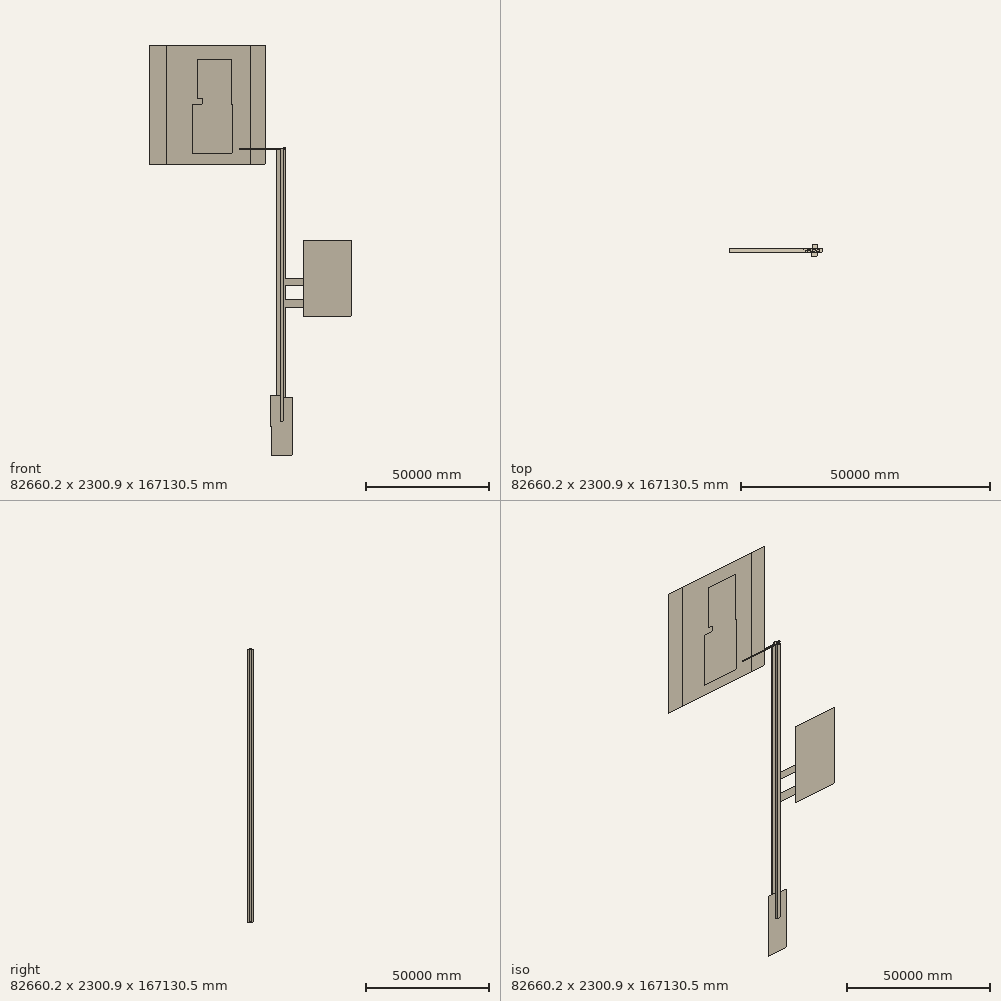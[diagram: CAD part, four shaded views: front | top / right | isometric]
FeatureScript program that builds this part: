
annotation { "Feature Type Name" : "Feature", "Feature Type Description" : "" }
export const myFeature = defineFeature(function(context is Context, id is Id, definition is map)
    precondition{}
    {
        {
            var Q0;
            Q0=qCreatedBy(makeId("Front.planeOp"),FACE);
            var sketch = newSketch(context, id + "F0", { "sketchPlane" : qUnion([Q0])});
            skLineSegment(sketch, "E0.bottom", {"start": v(-96.08, 96.62) * mm, "end": v(94.95, 96.62) * mm});
            skLineSegment(sketch, "E0.top", {"start": v(-96.08, -96.37) * mm, "end": v(94.95, -96.37) * mm});
            skLineSegment(sketch, "E0.left", {"start": v(-96.08, 96.62) * mm, "end": v(-96.08, -96.37) * mm});
            skLineSegment(sketch, "E0.right", {"start": v(94.95, 96.62) * mm, "end": v(94.95, -96.37) * mm});
            skSolve(sketch);
        }
        {
            var Q0;
            Q0 = qSketchRegion(id + "F0", true);
            extrude(context, id + "F1", {"entities" : qUnion([Q0]), "depth" : 25.4 * mm, "offsetDistance" : 25.4 * mm});
        }
        {
            var Q0;
            Q0=makeQuery(id+"F1.opExtrude","CAP_FACE",FACE,{"disambiguationData":[OSD([sQuery(id+"F0.wireOp",EDGE,"E0.bottom"),sQuery(id+"F0.wireOp",EDGE,"E0.top"),sQuery(id+"F0.wireOp",EDGE,"E0.left"),sQuery(id+"F0.wireOp",EDGE,"E0.right")])],"isStart":true});
            var sketch = newSketch(context, id + "F2", { "sketchPlane" : qUnion([Q0])});
            skLineSegment(sketch, "E1.bottom", {"start": v(0, 0) * mm, "end": v(76.12, 0) * mm});
            skLineSegment(sketch, "E1.top", {"start": v(0, 76.11) * mm, "end": v(76.12, 76.11) * mm});
            skLineSegment(sketch, "E1.left", {"start": v(0, 0) * mm, "end": v(0, 76.11) * mm});
            skLineSegment(sketch, "E1.right", {"start": v(76.12, 0) * mm, "end": v(76.12, 76.11) * mm});
            skLineSegment(sketch, "E2.bottom", {"start": v(76.12, 76.11) * mm, "end": v(-77.23, 76.11) * mm});
            skLineSegment(sketch, "E2.top", {"start": v(76.12, -75.62) * mm, "end": v(-77.23, -75.62) * mm});
            skLineSegment(sketch, "E2.left", {"start": v(76.12, 76.11) * mm, "end": v(76.12, -75.62) * mm});
            skLineSegment(sketch, "E2.right", {"start": v(-77.23, 76.11) * mm, "end": v(-77.23, -75.62) * mm});
            skSolve(sketch);
        }
        {
            var Q0;
            Q0 = qSketchRegion(id + "F2", true);
            extrude(context, id + "F3", {"entities" : qUnion([Q0]), "operationType" : NewBodyOperationType.ADD, "depth" : 25.4 * mm, "offsetDistance" : 25.4 * mm});
        }
        {
            var Q0;
            Q0=makeQuery(id+"F3.opExtrude","CAP_FACE",FACE,{"disambiguationData":[OSD([sQuery(id+"F2.wireOp",EDGE,"E2.bottom"),sQuery(id+"F2.wireOp",EDGE,"E2.top"),sQuery(id+"F2.wireOp",EDGE,"E2.left"),sQuery(id+"F2.wireOp",EDGE,"E2.right")])],"isStart":false});
            var sketch = newSketch(context, id + "F4", { "sketchPlane" : qUnion([Q0])});
            skLineSegment(sketch, "E3.bottom", {"start": v(97.63, 126.48) * mm, "end": v(-70.35, 126.48) * mm});
            skLineSegment(sketch, "E3.top", {"start": v(97.63, -97.82) * mm, "end": v(-70.35, -97.82) * mm});
            skLineSegment(sketch, "E3.left", {"start": v(97.63, 126.48) * mm, "end": v(97.63, -97.82) * mm});
            skLineSegment(sketch, "E3.right", {"start": v(-70.35, 126.48) * mm, "end": v(-70.35, -97.82) * mm});
            skLineSegment(sketch, "E4.bottom", {"start": v(-70.35, -97.82) * mm, "end": v(-97.74, -97.82) * mm});
            skLineSegment(sketch, "E4.top", {"start": v(-70.35, 96.2) * mm, "end": v(-97.74, 96.2) * mm});
            skLineSegment(sketch, "E4.left", {"start": v(-70.35, -97.82) * mm, "end": v(-70.35, 96.2) * mm});
            skLineSegment(sketch, "E4.right", {"start": v(-97.74, -97.82) * mm, "end": v(-97.74, 96.2) * mm});
            skSolve(sketch);
        }
        {
            var Q0;
            Q0 = qSketchRegion(id + "F4", true);
            extrude(context, id + "F5", {"entities" : qUnion([Q0]), "operationType" : NewBodyOperationType.ADD, "depth" : 25.4 * mm, "offsetDistance" : 25.4 * mm});
        }
        {
            var Q0;
            Q0=makeQuery(id+"F5.opExtrude","SWEPT_FACE",FACE,{"disambiguationData":[OSD([sQuery(id+"F4.wireOp",EDGE,"E4.top")])]});
            var sketch = newSketch(context, id + "F6", { "sketchPlane" : qUnion([Q0])});
            skLineSegment(sketch, "E5", {"start": v(97.74, 50.8) * mm, "end": v(97.74, 0) * mm});
            skLineSegment(sketch, "E6", {"start": v(97.74, 0) * mm, "end": v(48.7, -15.21) * mm});
            skLineSegment(sketch, "E7", {"start": v(48.7, -15.21) * mm, "end": v(97.74, 50.8) * mm});
            skLineSegment(sketch, "E8", {"start": v(48.7, -15.21) * mm, "end": v(70.35, 50.8) * mm});
            skSolve(sketch);
        }
        {
            var Q0;
            Q0 = qSketchRegion(id + "F6", true);
            extrude(context, id + "F7", {"entities" : qUnion([Q0]), "operationType" : NewBodyOperationType.ADD, "depth" : 25.4 * mm, "offsetDistance" : 25.4 * mm});
        }
        {
            var Q0;
            Q0=makeQuery(id+"F7.opExtrude","SWEPT_FACE",FACE,{"disambiguationData":[OSD([sQuery(id+"F6.wireOp",EDGE,"E7")])]});
            var sketch = newSketch(context, id + "F8", { "sketchPlane" : qUnion([Q0])});
            skLineSegment(sketch, "E9.bottom", {"start": v(-153.7, 205.91) * mm, "end": v(22.33, 205.91) * mm});
            skLineSegment(sketch, "E9.top", {"start": v(-153.7, 15.9) * mm, "end": v(22.33, 15.9) * mm});
            skLineSegment(sketch, "E9.left", {"start": v(-153.7, 205.91) * mm, "end": v(-153.7, 15.9) * mm});
            skLineSegment(sketch, "E9.right", {"start": v(22.33, 205.91) * mm, "end": v(22.33, 15.9) * mm});
            skLineSegment(sketch, "E10.bottom", {"start": v(22.33, 168.8) * mm, "end": v(22.33, 168.8) * mm});
            skLineSegment(sketch, "E10.top", {"start": v(22.33, 27.02) * mm, "end": v(22.33, 27.02) * mm});
            skLineSegment(sketch, "E10.left", {"start": v(22.33, 168.8) * mm, "end": v(22.33, 27.02) * mm});
            skLineSegment(sketch, "E10.right", {"start": v(22.33, 168.8) * mm, "end": v(22.33, 27.02) * mm});
            skSolve(sketch);
        }
        {
            var Q0;
            Q0 = qSketchRegion(id + "F8", true);
            extrude(context, id + "F9", {"entities" : qUnion([Q0]), "operationType" : NewBodyOperationType.ADD, "depth" : 25.4 * mm, "offsetDistance" : 25.4 * mm});
        }
        {
            var Q0;
            {var subQ0=sQuery(id+"F8.wireOp",EDGE,"E9.left");var subQ2=sQuery(id+"F8.wireOp",EDGE,"E9.bottom");var subQ5=sQuery(id+"F0.wireOp",EDGE,"E0.bottom");var subQ6=sQuery(id+"F8.wireOp",EDGE,"E9.top");var subQ7=sQuery(id+"F8.wireOp",EDGE,"E10.right");var subQ8=sQuery(id+"F8.wireOp",EDGE,"E9.right");Q0=makeQuery(id+"F9.boolean.opBoolean","SPLIT",FACE,{"disambiguationData":[TD([makeQuery(id+"F1.opExtrude","SWEPT_FACE",FACE,{"disambiguationData":[OSD([subQ5])]})])],"derivedFrom":makeQuery(id+"F9.opExtrude","CAP_FACE",FACE,{"disambiguationData":[OSD([subQ2,subQ6,subQ0,subQ8,subQ7])],"isStart":true})});}
            var sketch = newSketch(context, id + "F10", { "sketchPlane" : qUnion([Q0])});
            skLineSegment(sketch, "E11.bottom", {"start": v(-30.73, 15.9) * mm, "end": v(163.94, 15.9) * mm});
            skLineSegment(sketch, "E11.top", {"start": v(-30.73, 183.37) * mm, "end": v(163.94, 183.37) * mm});
            skLineSegment(sketch, "E11.left", {"start": v(-30.73, 15.9) * mm, "end": v(-30.73, 183.37) * mm});
            skLineSegment(sketch, "E11.right", {"start": v(163.94, 15.9) * mm, "end": v(163.94, 183.37) * mm});
            skLineSegment(sketch, "E12.bottom", {"start": v(-30.73, 183.37) * mm, "end": v(160.37, 183.37) * mm});
            skLineSegment(sketch, "E12.top", {"start": v(-30.73, 216.06) * mm, "end": v(160.37, 216.06) * mm});
            skLineSegment(sketch, "E12.left", {"start": v(-30.73, 183.37) * mm, "end": v(-30.73, 216.06) * mm});
            skLineSegment(sketch, "E12.right", {"start": v(160.37, 183.37) * mm, "end": v(160.37, 216.06) * mm});
            skSolve(sketch);
        }
        {
            var Q0;
            Q0 = qSketchRegion(id + "F10", true);
            extrude(context, id + "F11", {"entities" : qUnion([Q0]), "operationType" : NewBodyOperationType.ADD, "depth" : 25.4 * mm, "offsetDistance" : 25.4 * mm});
        }
        {
            var Q0;
            Q0=makeQuery(id+"F1.opExtrude","CAP_FACE",FACE,{"disambiguationData":[OSD([sQuery(id+"F0.wireOp",EDGE,"E0.bottom"),sQuery(id+"F0.wireOp",EDGE,"E0.top"),sQuery(id+"F0.wireOp",EDGE,"E0.left"),sQuery(id+"F0.wireOp",EDGE,"E0.right")])],"isStart":false});
            var sketch = newSketch(context, id + "F12", { "sketchPlane" : qUnion([Q0])});
            skLineSegment(sketch, "E13.bottom", {"start": v(0, 0) * mm, "end": v(9.48, 0) * mm});
            skLineSegment(sketch, "E13.top", {"start": v(0, 96.62) * mm, "end": v(9.48, 96.62) * mm});
            skLineSegment(sketch, "E13.left", {"start": v(0, 0) * mm, "end": v(0, 96.62) * mm});
            skLineSegment(sketch, "E13.right", {"start": v(9.48, 0) * mm, "end": v(9.48, 96.62) * mm});
            skLineSegment(sketch, "E14.bottom", {"start": v(9.48, 0) * mm, "end": v(-96.08, 0) * mm});
            skLineSegment(sketch, "E14.top", {"start": v(9.48, -96.37) * mm, "end": v(-96.08, -96.37) * mm});
            skLineSegment(sketch, "E14.left", {"start": v(9.48, 0) * mm, "end": v(9.48, -96.37) * mm});
            skLineSegment(sketch, "E14.right", {"start": v(-96.08, 0) * mm, "end": v(-96.08, -96.37) * mm});
            skLineSegment(sketch, "E15", {"start": v(9.48, 96.62) * mm, "end": v(-27.1, -27.97) * mm});
            skLineSegment(sketch, "E16", {"start": v(-27.1, -27.97) * mm, "end": v(44.8, -104.88) * mm});
            skLineSegment(sketch, "E17", {"start": v(44.8, -104.88) * mm, "end": v(125.25, -29.66) * mm});
            skLineSegment(sketch, "E18", {"start": v(125.25, -29.66) * mm, "end": v(80.32, 0) * mm});
            skLineSegment(sketch, "E19", {"start": v(80.32, 0) * mm, "end": v(9.48, 96.62) * mm});
            skSolve(sketch);
        }
        {
            var Q0;
            Q0 = qSketchRegion(id + "F12", true);
            extrude(context, id + "F13", {"entities" : qUnion([Q0]), "operationType" : NewBodyOperationType.ADD, "depth" : 25.4 * mm, "offsetDistance" : 25.4 * mm});
        }
        {
            var Q0;
            {var subQ0=sQuery(id+"F0.wireOp",EDGE,"E0.left");var subQ1=sQuery(id+"F0.wireOp",EDGE,"E0.bottom");Q0=makeQuery(id+"F13.boolean.opBoolean","SPLIT",FACE,{"disambiguationData":[TD([makeQuery(id+"F1.opExtrude","SWEPT_FACE",FACE,{"disambiguationData":[OSD([subQ0])]})])],"derivedFrom":makeQuery(id+"F1.opExtrude","CAP_FACE",FACE,{"disambiguationData":[OSD([subQ1,sQuery(id+"F0.wireOp",EDGE,"E0.top"),subQ0,sQuery(id+"F0.wireOp",EDGE,"E0.right")])],"isStart":false})});}
            var sketch = newSketch(context, id + "F14", { "sketchPlane" : qUnion([Q0])});
            skCircle(sketch, "E20", {"center": v(-47.68, 49.78) * mm, "radius": 38.28 * mm});
            skLineSegment(sketch, "E21.bottom", {"start": v(-18.9, 0) * mm, "end": v(-80.44, 0) * mm});
            skLineSegment(sketch, "E21.top", {"start": v(-18.9, -70.14) * mm, "end": v(-80.44, -70.14) * mm});
            skLineSegment(sketch, "E21.left", {"start": v(-18.9, 0) * mm, "end": v(-18.9, -70.14) * mm});
            skLineSegment(sketch, "E21.right", {"start": v(-80.44, 0) * mm, "end": v(-80.44, -70.14) * mm});
            skSolve(sketch);
        }
        {
            var Q0;
            Q0 = qSketchRegion(id + "F14", true);
            extrude(context, id + "F15", {"entities" : qUnion([Q0]), "operationType" : NewBodyOperationType.ADD, "depth" : 25.4 * mm, "offsetDistance" : 25.4 * mm});
        }
        {
            var Q0;
            Q0=makeQuery(id+"F5.opExtrude","CAP_FACE",FACE,{"disambiguationData":[OSD([sQuery(id+"F4.wireOp",EDGE,"E3.bottom"),sQuery(id+"F4.wireOp",EDGE,"E3.top"),sQuery(id+"F4.wireOp",EDGE,"E3.left"),sQuery(id+"F4.wireOp",EDGE,"E3.right"),sQuery(id+"F4.wireOp",EDGE,"E4.bottom"),sQuery(id+"F4.wireOp",EDGE,"E4.top"),sQuery(id+"F4.wireOp",EDGE,"E4.right")])],"isStart":false});
            var sketch = newSketch(context, id + "F16", { "sketchPlane" : qUnion([Q0])});
            skLineSegment(sketch, "E22.bottom", {"start": v(-9.65, -19.15) * mm, "end": v(-106, -19.15) * mm});
            skLineSegment(sketch, "E22.top", {"start": v(-9.65, 126.48) * mm, "end": v(-106, 126.48) * mm});
            skLineSegment(sketch, "E22.left", {"start": v(-9.65, -19.15) * mm, "end": v(-9.65, 126.48) * mm});
            skLineSegment(sketch, "E22.right", {"start": v(-106, -19.15) * mm, "end": v(-106, 126.48) * mm});
            skLineSegment(sketch, "E23.bottom", {"start": v(-9.65, 126.48) * mm, "end": v(107.3, 126.48) * mm});
            skLineSegment(sketch, "E23.top", {"start": v(-9.65, -78.96) * mm, "end": v(107.3, -78.96) * mm});
            skLineSegment(sketch, "E23.left", {"start": v(-9.65, 126.48) * mm, "end": v(-9.65, -78.96) * mm});
            skLineSegment(sketch, "E23.right", {"start": v(107.3, 126.48) * mm, "end": v(107.3, -78.96) * mm});
            skLineSegment(sketch, "E24.bottom", {"start": v(107.3, -78.96) * mm, "end": v(-106, -78.96) * mm});
            skLineSegment(sketch, "E24.top", {"start": v(107.3, -19.15) * mm, "end": v(-106, -19.15) * mm});
            skLineSegment(sketch, "E24.left", {"start": v(107.3, -78.96) * mm, "end": v(107.3, -19.15) * mm});
            skLineSegment(sketch, "E24.right", {"start": v(-106, -78.96) * mm, "end": v(-106, -19.15) * mm});
            skLineSegment(sketch, "E25.bottom", {"start": v(107.3, -78.96) * mm, "end": v(-107.64, -78.96) * mm});
            skLineSegment(sketch, "E25.top", {"start": v(107.3, -97.82) * mm, "end": v(-107.64, -97.82) * mm});
            skLineSegment(sketch, "E25.left", {"start": v(107.3, -78.96) * mm, "end": v(107.3, -97.82) * mm});
            skLineSegment(sketch, "E25.right", {"start": v(-107.64, -78.96) * mm, "end": v(-107.64, -97.82) * mm});
            skSolve(sketch);
        }
        {
            var Q0;
            Q0 = qSketchRegion(id + "F16", true);
            extrude(context, id + "F17", {"entities" : qUnion([Q0]), "operationType" : NewBodyOperationType.ADD, "depth" : 25.4 * mm, "offsetDistance" : 25.4 * mm});
        }
        {
            var Q0;
            Q0=makeQuery(id+"F17.opExtrude","CAP_FACE",FACE,{"disambiguationData":[OSD([sQuery(id+"F16.wireOp",EDGE,"E22.top"),sQuery(id+"F16.wireOp",EDGE,"E22.right"),sQuery(id+"F16.wireOp",EDGE,"E23.bottom"),sQuery(id+"F16.wireOp",EDGE,"E23.right"),sQuery(id+"F16.wireOp",EDGE,"E24.left"),sQuery(id+"F16.wireOp",EDGE,"E24.right"),sQuery(id+"F16.wireOp",EDGE,"E25.bottom"),sQuery(id+"F16.wireOp",EDGE,"E25.top"),sQuery(id+"F16.wireOp",EDGE,"E25.left"),sQuery(id+"F16.wireOp",EDGE,"E25.right")])],"isStart":false});
            var sketch = newSketch(context, id + "F18", { "sketchPlane" : qUnion([Q0])});
            skLineSegment(sketch, "E26.bottom", {"start": v(107.3, 126.48) * mm, "end": v(-107.64, 126.48) * mm});
            skLineSegment(sketch, "E26.top", {"start": v(107.3, -88.39) * mm, "end": v(-107.64, -88.39) * mm});
            skLineSegment(sketch, "E26.left", {"start": v(107.3, 126.48) * mm, "end": v(107.3, -88.39) * mm});
            skLineSegment(sketch, "E26.right", {"start": v(-107.64, 126.48) * mm, "end": v(-107.64, -88.39) * mm});
            skLineSegment(sketch, "E27.bottom", {"start": v(-107.64, 126.48) * mm, "end": v(63.7, 126.48) * mm});
            skLineSegment(sketch, "E27.top", {"start": v(-107.64, -88.39) * mm, "end": v(63.7, -88.39) * mm});
            skLineSegment(sketch, "E27.right", {"start": v(63.7, 126.48) * mm, "end": v(63.7, -88.39) * mm});
            skLineSegment(sketch, "E28.bottom", {"start": v(63.7, -88.39) * mm, "end": v(107.3, -88.39) * mm});
            skLineSegment(sketch, "E28.top", {"start": v(63.7, 126.48) * mm, "end": v(107.3, 126.48) * mm});
            skLineSegment(sketch, "E28.left", {"start": v(63.7, -88.39) * mm, "end": v(63.7, 126.48) * mm});
            skLineSegment(sketch, "E28.right", {"start": v(107.3, -88.39) * mm, "end": v(107.3, 126.48) * mm});
            skSolve(sketch);
        }
        {
            var Q0;
            Q0 = qSketchRegion(id + "F18", true);
            extrude(context, id + "F19", {"entities" : qUnion([Q0]), "operationType" : NewBodyOperationType.ADD, "depth" : 25.4 * mm, "offsetDistance" : 25.4 * mm});
        }
        {
            var Q0;
            Q0=makeQuery(id+"F19.opExtrude","CAP_FACE",FACE,{"disambiguationData":[OSD([sQuery(id+"F18.wireOp",EDGE,"E27.bottom"),sQuery(id+"F18.wireOp",EDGE,"E27.top"),sQuery(id+"F18.wireOp",EDGE,"E26.right"),sQuery(id+"F18.wireOp",EDGE,"E28.bottom"),sQuery(id+"F18.wireOp",EDGE,"E28.top"),sQuery(id+"F18.wireOp",EDGE,"E28.right")])],"isStart":false});
            var sketch = newSketch(context, id + "F20", { "sketchPlane" : qUnion([Q0])});
            skCircle(sketch, "E29", {"center": v(-17.74, 16.07) * mm, "radius": 55.57 * mm});
            skLineSegment(sketch, "E30.bottom", {"start": v(-103.84, 126.48) * mm, "end": v(107.3, 126.48) * mm});
            skLineSegment(sketch, "E30.top", {"start": v(-103.84, -88.39) * mm, "end": v(107.3, -88.39) * mm});
            skLineSegment(sketch, "E30.left", {"start": v(-103.84, 126.48) * mm, "end": v(-103.84, -88.39) * mm});
            skLineSegment(sketch, "E30.right", {"start": v(107.3, 126.48) * mm, "end": v(107.3, -88.39) * mm});
            skSolve(sketch);
        }
        {
            var Q0;
            Q0 = qSketchRegion(id + "F20", true);
            extrude(context, id + "F21", {"entities" : qUnion([Q0]), "operationType" : NewBodyOperationType.ADD, "depth" : 25.4 * mm, "offsetDistance" : 25.4 * mm});
        }
        {
            var Q0;
            Q0=makeQuery(id+"F21.boolean.opBoolean","SPLIT",FACE,{"disambiguationData":[TD([makeQuery(id+"F21.opExtrude","SWEPT_FACE",FACE,{"disambiguationData":[OSD([sQuery(id+"F20.wireOp",EDGE,"E29")])]})])],"derivedFrom":makeQuery(id+"F19.opExtrude","CAP_FACE",FACE,{"disambiguationData":[OSD([sQuery(id+"F18.wireOp",EDGE,"E27.bottom"),sQuery(id+"F18.wireOp",EDGE,"E27.top"),sQuery(id+"F18.wireOp",EDGE,"E26.right"),sQuery(id+"F18.wireOp",EDGE,"E28.bottom"),sQuery(id+"F18.wireOp",EDGE,"E28.top"),sQuery(id+"F18.wireOp",EDGE,"E28.right")])],"isStart":false})});
            var sketch = newSketch(context, id + "F22", { "sketchPlane" : qUnion([Q0])});
            skLineSegment(sketch, "E31.bottom", {"start": v(-17.74, 16.07) * mm, "end": v(22.45, 16.07) * mm});
            skLineSegment(sketch, "E31.top", {"start": v(-17.74, -22.32) * mm, "end": v(22.45, -22.32) * mm});
            skLineSegment(sketch, "E31.left", {"start": v(-17.74, 16.07) * mm, "end": v(-17.74, -22.32) * mm});
            skLineSegment(sketch, "E31.right", {"start": v(22.45, 16.07) * mm, "end": v(22.45, -22.32) * mm});
            skLineSegment(sketch, "E32.bottom", {"start": v(-17.74, 16.07) * mm, "end": v(-59.53, 16.07) * mm});
            skLineSegment(sketch, "E32.top", {"start": v(-17.74, 52.7) * mm, "end": v(-59.53, 52.7) * mm});
            skLineSegment(sketch, "E32.left", {"start": v(-17.74, 16.07) * mm, "end": v(-17.74, 52.7) * mm});
            skLineSegment(sketch, "E32.right", {"start": v(-59.53, 16.07) * mm, "end": v(-59.53, 52.7) * mm});
            skLineSegment(sketch, "E33.bottom", {"start": v(109, 130.29) * mm, "end": v(-103.23, 130.29) * mm});
            skLineSegment(sketch, "E33.top", {"start": v(109, -84.21) * mm, "end": v(-103.23, -84.21) * mm});
            skLineSegment(sketch, "E33.left", {"start": v(109, 130.29) * mm, "end": v(109, -84.21) * mm});
            skLineSegment(sketch, "E33.right", {"start": v(-103.23, 130.29) * mm, "end": v(-103.23, -84.21) * mm});
            skCircle(sketch, "E34", {"center": v(-17.74, 16.07) * mm, "radius": 60.52 * mm});
            skSolve(sketch);
        }
        {
            var Q0;
            Q0 = qSketchRegion(id + "F22", true);
            extrude(context, id + "F23", {"entities" : qUnion([Q0]), "operationType" : NewBodyOperationType.ADD, "depth" : 25.4 * mm, "offsetDistance" : 25.4 * mm});
        }
        {
            var Q0;
            Q0=makeQuery(id+"F23.boolean.opBoolean","MERGE",FACE,{"derivedFrom":[makeQuery(id+"F21.opExtrude","CAP_FACE",FACE,{"disambiguationData":[OSD([sQuery(id+"F20.wireOp",EDGE,"E29"),sQuery(id+"F20.wireOp",EDGE,"E30.bottom"),sQuery(id+"F20.wireOp",EDGE,"E30.top"),sQuery(id+"F20.wireOp",EDGE,"E30.left"),sQuery(id+"F20.wireOp",EDGE,"E30.right")])],"isStart":false}),makeQuery(id+"F23.opExtrude","CAP_FACE",FACE,{"disambiguationData":[OSD([sQuery(id+"F22.wireOp",EDGE,"E33.bottom"),sQuery(id+"F22.wireOp",EDGE,"E33.top"),sQuery(id+"F22.wireOp",EDGE,"E33.left"),sQuery(id+"F22.wireOp",EDGE,"E33.right"),sQuery(id+"F22.wireOp",EDGE,"E34")])],"isStart":false})]});
            var sketch = newSketch(context, id + "F24", { "sketchPlane" : qUnion([Q0])});
            skLineSegment(sketch, "E35.bottom", {"start": v(109, 130.29) * mm, "end": v(38.1, 130.29) * mm});
            skLineSegment(sketch, "E35.top", {"start": v(109, -88.39) * mm, "end": v(38.1, -88.39) * mm});
            skLineSegment(sketch, "E35.left", {"start": v(109, 130.29) * mm, "end": v(109, -88.39) * mm});
            skLineSegment(sketch, "E35.right", {"start": v(38.1, 130.29) * mm, "end": v(38.1, -88.39) * mm});
            skLineSegment(sketch, "E36.bottom", {"start": v(-103.84, -88.39) * mm, "end": v(-74.57, -88.39) * mm});
            skLineSegment(sketch, "E36.top", {"start": v(-103.84, 130.29) * mm, "end": v(-74.57, 130.29) * mm});
            skLineSegment(sketch, "E36.left", {"start": v(-103.84, -88.39) * mm, "end": v(-103.84, 130.29) * mm});
            skLineSegment(sketch, "E36.right", {"start": v(-74.57, -88.39) * mm, "end": v(-74.57, 130.29) * mm});
            skSolve(sketch);
        }
        {
            var Q0;
            Q0 = qSketchRegion(id + "F24", true);
            extrude(context, id + "F25", {"entities" : qUnion([Q0]), "operationType" : NewBodyOperationType.ADD, "depth" : 25.4 * mm, "offsetDistance" : 25.4 * mm});
        }
        {
            var Q0;
            Q0=makeQuery(id+"F25.opExtrude","CAP_FACE",FACE,{"disambiguationData":[OSD([sQuery(id+"F24.wireOp",EDGE,"E36.bottom"),sQuery(id+"F24.wireOp",EDGE,"E36.top"),sQuery(id+"F24.wireOp",EDGE,"E36.left"),sQuery(id+"F24.wireOp",EDGE,"E36.right")])],"isStart":false});
            var sketch = newSketch(context, id + "F26", { "sketchPlane" : qUnion([Q0])});
            skLineSegment(sketch, "E37.bottom", {"start": v(18.17, -85.22) * mm, "end": v(-195.24, -85.22) * mm});
            skLineSegment(sketch, "E37.top", {"start": v(18.17, 126.2) * mm, "end": v(-195.24, 126.2) * mm});
            skLineSegment(sketch, "E37.left", {"start": v(18.17, -85.22) * mm, "end": v(18.17, 126.2) * mm});
            skLineSegment(sketch, "E37.right", {"start": v(-195.24, -85.22) * mm, "end": v(-195.24, 126.2) * mm});
            skCircle(sketch, "E38", {"center": v(0, -23.55) * mm, "radius": 63.44 * mm});
            skSolve(sketch);
        }
        {
            var Q0;
            Q0 = qSketchRegion(id + "F26", true);
            extrude(context, id + "F27", {"entities" : qUnion([Q0]), "operationType" : NewBodyOperationType.ADD, "depth" : 25.4 * mm, "offsetDistance" : 25.4 * mm});
        }
        {
            var Q0;
            Q0=makeQuery(id+"F27.opExtrude","CAP_FACE",FACE,{"disambiguationData":[OSD([sQuery(id+"F26.wireOp",EDGE,"E37.bottom"),sQuery(id+"F26.wireOp",EDGE,"E37.top"),sQuery(id+"F26.wireOp",EDGE,"E37.left"),sQuery(id+"F26.wireOp",EDGE,"E37.right"),sQuery(id+"F26.wireOp",EDGE,"E38")])],"isStart":false});
            var sketch = newSketch(context, id + "F28", { "sketchPlane" : qUnion([Q0])});
            skCircle(sketch, "E39", {"center": v(-90.12, 20.45) * mm, "radius": 81.64 * mm});
            skLineSegment(sketch, "E40.bottom", {"start": v(18.17, -85.22) * mm, "end": v(-150.47, -85.22) * mm});
            skLineSegment(sketch, "E40.top", {"start": v(18.17, 49.73) * mm, "end": v(-150.47, 49.73) * mm});
            skLineSegment(sketch, "E40.left", {"start": v(18.17, -85.22) * mm, "end": v(18.17, 49.73) * mm});
            skLineSegment(sketch, "E40.right", {"start": v(-150.47, -85.22) * mm, "end": v(-150.47, 49.73) * mm});
            skLineSegment(sketch, "E41.bottom", {"start": v(-150.47, 49.73) * mm, "end": v(14.85, 49.73) * mm});
            skLineSegment(sketch, "E41.top", {"start": v(-150.47, -85.22) * mm, "end": v(14.85, -85.22) * mm});
            skLineSegment(sketch, "E41.left", {"start": v(-150.47, 49.73) * mm, "end": v(-150.47, -85.22) * mm});
            skLineSegment(sketch, "E41.right", {"start": v(14.85, 49.73) * mm, "end": v(14.85, -85.22) * mm});
            skLineSegment(sketch, "E42.bottom", {"start": v(14.85, -85.22) * mm, "end": v(-147.42, -85.22) * mm});
            skLineSegment(sketch, "E42.top", {"start": v(14.85, -176.52) * mm, "end": v(-147.42, -176.52) * mm});
            skLineSegment(sketch, "E42.left", {"start": v(14.85, -85.22) * mm, "end": v(14.85, -176.52) * mm});
            skLineSegment(sketch, "E42.right", {"start": v(-147.42, -85.22) * mm, "end": v(-147.42, -176.52) * mm});
            skLineSegment(sketch, "E43.bottom", {"start": v(14.85, -176.52) * mm, "end": v(94.58, -176.52) * mm});
            skLineSegment(sketch, "E43.top", {"start": v(14.85, -231.27) * mm, "end": v(94.58, -231.27) * mm});
            skLineSegment(sketch, "E43.left", {"start": v(14.85, -176.52) * mm, "end": v(14.85, -231.27) * mm});
            skLineSegment(sketch, "E43.right", {"start": v(94.58, -176.52) * mm, "end": v(94.58, -231.27) * mm});
            skLineSegment(sketch, "E44.bottom", {"start": v(94.58, -176.52) * mm, "end": v(14.85, -176.52) * mm});
            skLineSegment(sketch, "E44.top", {"start": v(94.58, -85.22) * mm, "end": v(14.85, -85.22) * mm});
            skLineSegment(sketch, "E44.left", {"start": v(94.58, -176.52) * mm, "end": v(94.58, -85.22) * mm});
            skLineSegment(sketch, "E44.right", {"start": v(14.85, -176.52) * mm, "end": v(14.85, -85.22) * mm});
            skSolve(sketch);
        }
        {
            var Q0;
            Q0 = qSketchRegion(id + "F28", true);
            extrude(context, id + "F29", {"entities" : qUnion([Q0]), "operationType" : NewBodyOperationType.ADD, "depth" : 25.4 * mm, "offsetDistance" : 25.4 * mm});
        }
        {
            var Q0;
            {var subQ0=sQuery(id+"F26.wireOp",EDGE,"E37.left");var subQ1=sQuery(id+"F26.wireOp",EDGE,"E37.bottom");var subQ2=sQuery(id+"F26.wireOp",EDGE,"E38");var subQ3=makeQuery(id+"F26.imprint","INTERSECT",VERTEX,{"disambiguationData":[OD(0.0)],"derivedFrom":[subQ0,subQ2]});var subQ4=sQuery(id+"F26.wireOp",EDGE,"E37.top");Q0=makeQuery(id+"F29.boolean.opBoolean","SPLIT",FACE,{"disambiguationData":[TD([makeQuery(id+"F27.opExtrude","SWEPT_FACE",FACE,{"disambiguationData":[OSD([subQ2]),TDD([makeQuery(id+"F26.imprint","IMPRINT",EDGE,{"disambiguationData":[TD([[subQ3,-1.0]])],"derivedFrom":subQ2})])]})])],"derivedFrom":makeQuery(id+"F27.opExtrude","CAP_FACE",FACE,{"disambiguationData":[OSD([subQ1,subQ4,subQ0,sQuery(id+"F26.wireOp",EDGE,"E37.right"),subQ2])],"isStart":false})});}
            var sketch = newSketch(context, id + "F30", { "sketchPlane" : qUnion([Q0])});
            skCircle(sketch, "E45", {"center": v(18.17, -10.57) * mm, "radius": 24.04 * mm});
            skSolve(sketch);
        }
        {
            var Q0;
            Q0 = qSketchRegion(id + "F30", true);
            extrude(context, id + "F31", {"entities" : qUnion([Q0]), "operationType" : NewBodyOperationType.ADD, "depth" : 25.4 * mm, "offsetDistance" : 25.4 * mm});
        }
        {
            var Q0;
            Q0=makeQuery(id+"F29.opExtrude","CAP_FACE",FACE,{"disambiguationData":[OSD([sQuery(id+"F28.wireOp",EDGE,"E39"),sQuery(id+"F28.wireOp",EDGE,"E40.top"),sQuery(id+"F28.wireOp",EDGE,"E40.left"),sQuery(id+"F28.wireOp",EDGE,"E41.bottom"),sQuery(id+"F28.wireOp",EDGE,"E41.top"),sQuery(id+"F28.wireOp",EDGE,"E41.left"),sQuery(id+"F28.wireOp",EDGE,"E42.top"),sQuery(id+"F28.wireOp",EDGE,"E42.right"),sQuery(id+"F28.wireOp",EDGE,"E43.top"),sQuery(id+"F28.wireOp",EDGE,"E43.left"),sQuery(id+"F28.wireOp",EDGE,"E43.right"),sQuery(id+"F28.wireOp",EDGE,"E44.top"),sQuery(id+"F28.wireOp",EDGE,"E44.left")])],"isStart":true});
            var sketch = newSketch(context, id + "F32", { "sketchPlane" : qUnion([Q0])});
            skLineSegment(sketch, "E46.bottom", {"start": v(-80.23, -52.67) * mm, "end": v(43.1, -52.67) * mm});
            skLineSegment(sketch, "E46.top", {"start": v(-80.23, -265) * mm, "end": v(43.1, -265) * mm});
            skLineSegment(sketch, "E46.left", {"start": v(-80.23, -52.67) * mm, "end": v(-80.23, -265) * mm});
            skLineSegment(sketch, "E46.right", {"start": v(43.1, -52.67) * mm, "end": v(43.1, -265) * mm});
            skLineSegment(sketch, "E47.bottom", {"start": v(43.1, -52.67) * mm, "end": v(43.1, -52.67) * mm});
            skLineSegment(sketch, "E47.top", {"start": v(43.1, -265) * mm, "end": v(43.1, -265) * mm});
            skSolve(sketch);
        }
        {
            var Q0;
            Q0 = qSketchRegion(id + "F32", true);
            extrude(context, id + "F33", {"entities" : qUnion([Q0]), "operationType" : NewBodyOperationType.ADD, "depth" : 25.4 * mm, "offsetDistance" : 25.4 * mm});
        }
        {
            var Q0;
            Q0=makeQuery(id+"F33.boolean.opBoolean","SPLIT",FACE,{"derivedFrom":makeQuery(id+"F33.opExtrude","CAP_FACE",FACE,{"disambiguationData":[OSD([sQuery(id+"F32.wireOp",EDGE,"E46.bottom"),sQuery(id+"F32.wireOp",EDGE,"E46.top"),sQuery(id+"F32.wireOp",EDGE,"E46.left"),sQuery(id+"F32.wireOp",EDGE,"E46.right")])],"isStart":true})});
            var sketch = newSketch(context, id + "F34", { "sketchPlane" : qUnion([Q0])});
            skLineSegment(sketch, "E48.bottom", {"start": v(-88.1, -326.4) * mm, "end": v(126, -326.4) * mm});
            skLineSegment(sketch, "E48.top", {"start": v(-88.1, -114.28) * mm, "end": v(126, -114.28) * mm});
            skLineSegment(sketch, "E48.left", {"start": v(-88.1, -326.4) * mm, "end": v(-88.1, -114.28) * mm});
            skLineSegment(sketch, "E48.right", {"start": v(126, -326.4) * mm, "end": v(126, -114.28) * mm});
            skSolve(sketch);
        }
        {
            var Q0;
            Q0 = qSketchRegion(id + "F34", true);
            extrude(context, id + "F35", {"entities" : qUnion([Q0]), "operationType" : NewBodyOperationType.ADD, "depth" : 25.4 * mm, "offsetDistance" : 25.4 * mm});
        }
        {
            var Q0;
            Q0=makeQuery(id+"F35.boolean.opBoolean","MERGE",FACE,{"derivedFrom":[makeQuery(id+"F31.boolean.opBoolean","MERGE",FACE,{"derivedFrom":[makeQuery(id+"F29.opExtrude","CAP_FACE",FACE,{"disambiguationData":[OSD([sQuery(id+"F28.wireOp",EDGE,"E39"),sQuery(id+"F28.wireOp",EDGE,"E40.top"),sQuery(id+"F28.wireOp",EDGE,"E40.left"),sQuery(id+"F28.wireOp",EDGE,"E41.bottom"),sQuery(id+"F28.wireOp",EDGE,"E41.top"),sQuery(id+"F28.wireOp",EDGE,"E41.left"),sQuery(id+"F28.wireOp",EDGE,"E42.top"),sQuery(id+"F28.wireOp",EDGE,"E42.right"),sQuery(id+"F28.wireOp",EDGE,"E43.top"),sQuery(id+"F28.wireOp",EDGE,"E43.left"),sQuery(id+"F28.wireOp",EDGE,"E43.right"),sQuery(id+"F28.wireOp",EDGE,"E44.top"),sQuery(id+"F28.wireOp",EDGE,"E44.left")])],"isStart":false}),makeQuery(id+"F31.opExtrude","CAP_FACE",FACE,{"disambiguationData":[OSD([sQuery(id+"F30.wireOp",EDGE,"E45")])],"isStart":false})]}),makeQuery(id+"F35.opExtrude","CAP_FACE",FACE,{"disambiguationData":[OSD([sQuery(id+"F34.wireOp",EDGE,"E48.bottom"),sQuery(id+"F34.wireOp",EDGE,"E48.top"),sQuery(id+"F34.wireOp",EDGE,"E48.left"),sQuery(id+"F34.wireOp",EDGE,"E48.right")])],"isStart":false})]});
            var sketch = newSketch(context, id + "F36", { "sketchPlane" : qUnion([Q0])});
            skLineSegment(sketch, "E49.bottom", {"start": v(-202.61, 66.2) * mm, "end": v(158.45, 66.2) * mm});
            skLineSegment(sketch, "E49.top", {"start": v(-202.61, -293.1) * mm, "end": v(158.45, -293.1) * mm});
            skLineSegment(sketch, "E49.left", {"start": v(-202.61, 66.2) * mm, "end": v(-202.61, -293.1) * mm});
            skLineSegment(sketch, "E49.right", {"start": v(158.45, 66.2) * mm, "end": v(158.45, -293.1) * mm});
            skSolve(sketch);
        }
        {
            var Q0;
            Q0 = qSketchRegion(id + "F36", true);
            extrude(context, id + "F37", {"entities" : qUnion([Q0]), "operationType" : NewBodyOperationType.ADD, "depth" : 25.4 * mm, "offsetDistance" : 25.4 * mm});
        }
        {
            var Q0;
            Q0=makeQuery(id+"F37.opExtrude","SWEPT_FACE",FACE,{"disambiguationData":[OSD([sQuery(id+"F36.wireOp",EDGE,"E49.bottom")])]});
            var sketch = newSketch(context, id + "F38", { "sketchPlane" : qUnion([Q0])});
            skLineSegment(sketch, "E50.bottom", {"start": v(-154.41, 37.16) * mm, "end": v(199.37, 37.16) * mm});
            skLineSegment(sketch, "E50.top", {"start": v(-154.41, 393.07) * mm, "end": v(199.37, 393.07) * mm});
            skLineSegment(sketch, "E50.left", {"start": v(-154.41, 37.16) * mm, "end": v(-154.41, 393.07) * mm});
            skLineSegment(sketch, "E50.right", {"start": v(199.37, 37.16) * mm, "end": v(199.37, 393.07) * mm});
            skSolve(sketch);
        }
        {
            var Q0;
            Q0 = qSketchRegion(id + "F38", true);
            extrude(context, id + "F39", {"entities" : qUnion([Q0]), "operationType" : NewBodyOperationType.ADD, "depth" : 25.4 * mm, "offsetDistance" : 25.4 * mm});
        }
        {
            var Q0;
            Q0=makeQuery(id+"F37.opExtrude","CAP_FACE",FACE,{"disambiguationData":[OSD([sQuery(id+"F36.wireOp",EDGE,"E49.bottom"),sQuery(id+"F36.wireOp",EDGE,"E49.top"),sQuery(id+"F36.wireOp",EDGE,"E49.left"),sQuery(id+"F36.wireOp",EDGE,"E49.right")])],"isStart":false});
            var sketch = newSketch(context, id + "F40", { "sketchPlane" : qUnion([Q0])});
            skLineSegment(sketch, "E51.bottom", {"start": v(-199.37, 66.2) * mm, "end": v(158.45, 66.2) * mm});
            skLineSegment(sketch, "E51.top", {"start": v(-199.37, -293.1) * mm, "end": v(158.45, -293.1) * mm});
            skLineSegment(sketch, "E51.left", {"start": v(-199.37, 66.2) * mm, "end": v(-199.37, -293.1) * mm});
            skLineSegment(sketch, "E51.right", {"start": v(158.45, 66.2) * mm, "end": v(158.45, -293.1) * mm});
            skSolve(sketch);
        }
        {
            var Q0;
            Q0 = qSketchRegion(id + "F40", true);
            extrude(context, id + "F41", {"entities" : qUnion([Q0]), "operationType" : NewBodyOperationType.ADD, "depth" : 25.4 * mm, "offsetDistance" : 25.4 * mm});
        }
        {
            var Q0;
            Q0=makeQuery(id+"F41.opExtrude","CAP_FACE",FACE,{"disambiguationData":[OSD([sQuery(id+"F40.wireOp",EDGE,"E51.bottom"),sQuery(id+"F40.wireOp",EDGE,"E51.top"),sQuery(id+"F40.wireOp",EDGE,"E51.left"),sQuery(id+"F40.wireOp",EDGE,"E51.right")])],"isStart":false});
            var sketch = newSketch(context, id + "F42", { "sketchPlane" : qUnion([Q0])});
            skLineSegment(sketch, "E52.bottom", {"start": v(-199.37, 66.2) * mm, "end": v(158.45, 66.2) * mm});
            skLineSegment(sketch, "E52.top", {"start": v(-199.37, -293.1) * mm, "end": v(158.45, -293.1) * mm});
            skLineSegment(sketch, "E52.left", {"start": v(-199.37, 66.2) * mm, "end": v(-199.37, -293.1) * mm});
            skLineSegment(sketch, "E52.right", {"start": v(158.45, 66.2) * mm, "end": v(158.45, -293.1) * mm});
            skSolve(sketch);
        }
        {
            var Q0;
            Q0 = qSketchRegion(id + "F42", true);
            extrude(context, id + "F43", {"entities" : qUnion([Q0]), "operationType" : NewBodyOperationType.ADD, "depth" : 25.4 * mm, "offsetDistance" : 25.4 * mm});
        }
        {
            var Q0;
            Q0=makeQuery(id+"F43.opExtrude","CAP_FACE",FACE,{"disambiguationData":[OSD([sQuery(id+"F42.wireOp",EDGE,"E52.bottom"),sQuery(id+"F42.wireOp",EDGE,"E52.top"),sQuery(id+"F42.wireOp",EDGE,"E52.left"),sQuery(id+"F42.wireOp",EDGE,"E52.right")])],"isStart":false});
            var sketch = newSketch(context, id + "F44", { "sketchPlane" : qUnion([Q0])});
            skLineSegment(sketch, "E53.bottom", {"start": v(-199.37, 66.2) * mm, "end": v(158.45, 66.2) * mm});
            skLineSegment(sketch, "E53.top", {"start": v(-199.37, -293.1) * mm, "end": v(158.45, -293.1) * mm});
            skLineSegment(sketch, "E53.left", {"start": v(-199.37, 66.2) * mm, "end": v(-199.37, -293.1) * mm});
            skLineSegment(sketch, "E53.right", {"start": v(158.45, 66.2) * mm, "end": v(158.45, -293.1) * mm});
            skSolve(sketch);
        }
        {
            var Q0;
            Q0 = qSketchRegion(id + "F44", true);
            extrude(context, id + "F45", {"entities" : qUnion([Q0]), "operationType" : NewBodyOperationType.ADD, "depth" : 25.4 * mm, "offsetDistance" : 25.4 * mm});
        }
        {
            var Q0;
            Q0=makeQuery(id+"F45.opExtrude","CAP_FACE",FACE,{"disambiguationData":[OSD([sQuery(id+"F44.wireOp",EDGE,"E53.bottom"),sQuery(id+"F44.wireOp",EDGE,"E53.top"),sQuery(id+"F44.wireOp",EDGE,"E53.left"),sQuery(id+"F44.wireOp",EDGE,"E53.right")])],"isStart":false});
            var sketch = newSketch(context, id + "F46", { "sketchPlane" : qUnion([Q0])});
            skLineSegment(sketch, "E54.bottom", {"start": v(-199.37, 66.2) * mm, "end": v(158.45, 66.2) * mm});
            skLineSegment(sketch, "E54.top", {"start": v(-199.37, -293.1) * mm, "end": v(158.45, -293.1) * mm});
            skLineSegment(sketch, "E54.left", {"start": v(-199.37, 66.2) * mm, "end": v(-199.37, -293.1) * mm});
            skLineSegment(sketch, "E54.right", {"start": v(158.45, 66.2) * mm, "end": v(158.45, -293.1) * mm});
            skSolve(sketch);
        }
        {
            var Q0;
            Q0 = qSketchRegion(id + "F46", true);
            extrude(context, id + "F47", {"entities" : qUnion([Q0]), "operationType" : NewBodyOperationType.ADD, "depth" : 25.4 * mm, "offsetDistance" : 25.4 * mm});
        }
        {
            var Q0;
            Q0=makeQuery(id+"F47.opExtrude","CAP_FACE",FACE,{"disambiguationData":[OSD([sQuery(id+"F46.wireOp",EDGE,"E54.bottom"),sQuery(id+"F46.wireOp",EDGE,"E54.top"),sQuery(id+"F46.wireOp",EDGE,"E54.left"),sQuery(id+"F46.wireOp",EDGE,"E54.right")])],"isStart":false});
            var sketch = newSketch(context, id + "F48", { "sketchPlane" : qUnion([Q0])});
            skLineSegment(sketch, "E55.bottom", {"start": v(-199.37, -293.1) * mm, "end": v(158.45, -293.1) * mm});
            skLineSegment(sketch, "E55.top", {"start": v(-199.37, 66.2) * mm, "end": v(158.45, 66.2) * mm});
            skLineSegment(sketch, "E55.left", {"start": v(-199.37, -293.1) * mm, "end": v(-199.37, 66.2) * mm});
            skLineSegment(sketch, "E55.right", {"start": v(158.45, -293.1) * mm, "end": v(158.45, 66.2) * mm});
            skSolve(sketch);
        }
        {
            var Q0;
            Q0 = qSketchRegion(id + "F48", true);
            extrude(context, id + "F49", {"entities" : qUnion([Q0]), "operationType" : NewBodyOperationType.ADD, "depth" : 25.4 * mm, "offsetDistance" : 25.4 * mm});
        }
        {
            var Q0;
            Q0=makeQuery(id+"F49.opExtrude","CAP_FACE",FACE,{"disambiguationData":[OSD([sQuery(id+"F48.wireOp",EDGE,"E55.bottom"),sQuery(id+"F48.wireOp",EDGE,"E55.top"),sQuery(id+"F48.wireOp",EDGE,"E55.left"),sQuery(id+"F48.wireOp",EDGE,"E55.right")])],"isStart":false});
            var sketch = newSketch(context, id + "F50", { "sketchPlane" : qUnion([Q0])});
            skLineSegment(sketch, "E56.bottom", {"start": v(154.41, 66.2) * mm, "end": v(-199.37, 66.2) * mm});
            skLineSegment(sketch, "E56.top", {"start": v(154.41, -293.1) * mm, "end": v(-199.37, -293.1) * mm});
            skLineSegment(sketch, "E56.left", {"start": v(154.41, 66.2) * mm, "end": v(154.41, -293.1) * mm});
            skLineSegment(sketch, "E56.right", {"start": v(-199.37, 66.2) * mm, "end": v(-199.37, -293.1) * mm});
            skSolve(sketch);
        }
        {
            var Q0;
            Q0 = qSketchRegion(id + "F50", true);
            extrude(context, id + "F51", {"entities" : qUnion([Q0]), "operationType" : NewBodyOperationType.ADD, "depth" : 25.4 * mm, "offsetDistance" : 25.4 * mm});
        }
        {
            var Q0;
            Q0=makeQuery(id+"F51.opExtrude","CAP_FACE",FACE,{"disambiguationData":[OSD([sQuery(id+"F50.wireOp",EDGE,"E56.bottom"),sQuery(id+"F50.wireOp",EDGE,"E56.top"),sQuery(id+"F50.wireOp",EDGE,"E56.left"),sQuery(id+"F50.wireOp",EDGE,"E56.right")])],"isStart":false});
            var sketch = newSketch(context, id + "F52", { "sketchPlane" : qUnion([Q0])});
            skLineSegment(sketch, "E57.bottom", {"start": v(-199.37, 66.2) * mm, "end": v(-68.61, 66.2) * mm});
            skLineSegment(sketch, "E57.top", {"start": v(-199.37, -293.1) * mm, "end": v(-68.61, -293.1) * mm});
            skLineSegment(sketch, "E57.left", {"start": v(-199.37, 66.2) * mm, "end": v(-199.37, -293.1) * mm});
            skLineSegment(sketch, "E57.right", {"start": v(-68.61, 66.2) * mm, "end": v(-68.61, -293.1) * mm});
            skLineSegment(sketch, "E58.bottom", {"start": v(-68.61, 66.2) * mm, "end": v(60.26, 66.2) * mm});
            skLineSegment(sketch, "E58.top", {"start": v(-68.61, -154.4) * mm, "end": v(60.26, -154.4) * mm});
            skLineSegment(sketch, "E58.left", {"start": v(-68.61, 66.2) * mm, "end": v(-68.61, -154.4) * mm});
            skLineSegment(sketch, "E58.right", {"start": v(60.26, 66.2) * mm, "end": v(60.26, -154.4) * mm});
            skLineSegment(sketch, "E59.bottom", {"start": v(122.75, -81.4) * mm, "end": v(-81.47, -81.4) * mm});
            skLineSegment(sketch, "E59.top", {"start": v(122.75, -293.1) * mm, "end": v(-81.47, -293.1) * mm});
            skLineSegment(sketch, "E59.left", {"start": v(122.75, -81.4) * mm, "end": v(122.75, -293.1) * mm});
            skLineSegment(sketch, "E59.right", {"start": v(-81.47, -81.4) * mm, "end": v(-81.47, -293.1) * mm});
            skSolve(sketch);
        }
        {
            var Q0;
            Q0 = qSketchRegion(id + "F52", true);
            extrude(context, id + "F53", {"entities" : qUnion([Q0]), "operationType" : NewBodyOperationType.ADD, "depth" : 25.4 * mm, "offsetDistance" : 25.4 * mm});
        }
        {
            var Q0;
            Q0=makeQuery(id+"F53.opExtrude","CAP_FACE",FACE,{"disambiguationData":[OSD([sQuery(id+"F52.wireOp",EDGE,"E57.bottom"),sQuery(id+"F52.wireOp",EDGE,"E57.top"),sQuery(id+"F52.wireOp",EDGE,"E57.left"),sQuery(id+"F52.wireOp",EDGE,"E58.bottom"),sQuery(id+"F52.wireOp",EDGE,"E58.right"),sQuery(id+"F52.wireOp",EDGE,"E59.bottom"),sQuery(id+"F52.wireOp",EDGE,"E59.top"),sQuery(id+"F52.wireOp",EDGE,"E59.left")])],"isStart":false});
            var sketch = newSketch(context, id + "F54", { "sketchPlane" : qUnion([Q0])});
            skLineSegment(sketch, "E60.bottom", {"start": v(-217.08, 66.2) * mm, "end": v(143.54, 66.2) * mm});
            skLineSegment(sketch, "E60.top", {"start": v(-217.08, -293.1) * mm, "end": v(143.54, -293.1) * mm});
            skLineSegment(sketch, "E60.left", {"start": v(-217.08, 66.2) * mm, "end": v(-217.08, -293.1) * mm});
            skLineSegment(sketch, "E60.right", {"start": v(143.54, 66.2) * mm, "end": v(143.54, -293.1) * mm});
            skSolve(sketch);
        }
        {
            var Q0;
            Q0 = qSketchRegion(id + "F54", true);
            extrude(context, id + "F55", {"entities" : qUnion([Q0]), "operationType" : NewBodyOperationType.ADD, "depth" : 25.4 * mm, "offsetDistance" : 25.4 * mm});
        }
        {
            var Q0;
            Q0=makeQuery(id+"F55.opExtrude","CAP_FACE",FACE,{"disambiguationData":[OSD([sQuery(id+"F54.wireOp",EDGE,"E60.bottom"),sQuery(id+"F54.wireOp",EDGE,"E60.top"),sQuery(id+"F54.wireOp",EDGE,"E60.left"),sQuery(id+"F54.wireOp",EDGE,"E60.right")])],"isStart":false});
            var sketch = newSketch(context, id + "F56", { "sketchPlane" : qUnion([Q0])});
            skCircle(sketch, "E61", {"center": v(47.18, -113.46) * mm, "radius": 93.48 * mm});
            skPoint(sketch, "E61.centerSnap0", {"position": v(143.54, -113.46) * mm});
            skLineSegment(sketch, "E62.bottom", {"start": v(210.9, 135.17) * mm, "end": v(-268.99, 135.17) * mm});
            skLineSegment(sketch, "E62.top", {"start": v(210.9, -329.4) * mm, "end": v(-268.99, -329.4) * mm});
            skLineSegment(sketch, "E62.left", {"start": v(210.9, 135.17) * mm, "end": v(210.9, -329.4) * mm});
            skLineSegment(sketch, "E62.right", {"start": v(-268.99, 135.17) * mm, "end": v(-268.99, -329.4) * mm});
            skLineSegment(sketch, "E63.bottom", {"start": v(-268.99, 135.17) * mm, "end": v(-268.99, 135.17) * mm});
            skLineSegment(sketch, "E63.top", {"start": v(-268.99, -329.4) * mm, "end": v(-268.99, -329.4) * mm});
            skLineSegment(sketch, "E64.top", {"start": v(-268.99, -291.75) * mm, "end": v(-268.99, -291.75) * mm});
            skLineSegment(sketch, "E64.left", {"start": v(-268.99, 135.17) * mm, "end": v(-268.99, -291.75) * mm});
            skLineSegment(sketch, "E64.right", {"start": v(-268.99, 135.17) * mm, "end": v(-268.99, -291.75) * mm});
            skLineSegment(sketch, "E65.left", {"start": v(-268.99, -291.75) * mm, "end": v(-268.99, 135.17) * mm});
            skLineSegment(sketch, "E65.right", {"start": v(-268.99, -291.75) * mm, "end": v(-268.99, 135.17) * mm});
            skSolve(sketch);
        }
        {
            var Q0;
            Q0 = qSketchRegion(id + "F56", true);
            extrude(context, id + "F57", {"entities" : qUnion([Q0]), "operationType" : NewBodyOperationType.ADD, "depth" : 25.4 * mm, "offsetDistance" : 25.4 * mm});
        }
        {
            var Q0;
            Q0=makeQuery(id+"F57.opExtrude","CAP_FACE",FACE,{"disambiguationData":[OSD([sQuery(id+"F56.wireOp",EDGE,"E61"),sQuery(id+"F56.wireOp",EDGE,"E62.bottom"),sQuery(id+"F56.wireOp",EDGE,"E62.top"),sQuery(id+"F56.wireOp",EDGE,"E62.left"),sQuery(id+"F56.wireOp",EDGE,"E62.right"),sQuery(id+"F56.wireOp",EDGE,"E65.right")])],"isStart":false});
            var sketch = newSketch(context, id + "F58", { "sketchPlane" : qUnion([Q0])});
            skLineSegment(sketch, "E66.bottom", {"start": v(210.9, -353.4) * mm, "end": v(-251.82, -353.4) * mm});
            skLineSegment(sketch, "E66.top", {"start": v(210.9, 135.17) * mm, "end": v(-251.82, 135.17) * mm});
            skLineSegment(sketch, "E66.left", {"start": v(210.9, -353.4) * mm, "end": v(210.9, 135.17) * mm});
            skLineSegment(sketch, "E66.right", {"start": v(-251.82, -353.4) * mm, "end": v(-251.82, 135.17) * mm});
            skCircle(sketch, "E67", {"center": v(47.18, -113.46) * mm, "radius": 92.85 * mm});
            skSolve(sketch);
        }
        {
            var Q0;
            Q0 = qSketchRegion(id + "F58", true);
            extrude(context, id + "F59", {"entities" : qUnion([Q0]), "operationType" : NewBodyOperationType.ADD, "depth" : 25.4 * mm, "offsetDistance" : 25.4 * mm});
        }
        {
            var Q0;
            Q0=makeQuery(id+"F59.opExtrude","CAP_FACE",FACE,{"disambiguationData":[OSD([sQuery(id+"F58.wireOp",EDGE,"E66.bottom"),sQuery(id+"F58.wireOp",EDGE,"E66.top"),sQuery(id+"F58.wireOp",EDGE,"E66.left"),sQuery(id+"F58.wireOp",EDGE,"E66.right"),sQuery(id+"F58.wireOp",EDGE,"E67")])],"isStart":false});
            var sketch = newSketch(context, id + "F60", { "sketchPlane" : qUnion([Q0])});
            skLineSegment(sketch, "E68.bottom", {"start": v(210.9, -353.4) * mm, "end": v(231.22, -353.4) * mm});
            skLineSegment(sketch, "E68.top", {"start": v(210.9, 135.17) * mm, "end": v(231.22, 135.17) * mm});
            skLineSegment(sketch, "E68.left", {"start": v(210.9, -353.4) * mm, "end": v(210.9, 135.17) * mm});
            skLineSegment(sketch, "E68.right", {"start": v(231.22, -353.4) * mm, "end": v(231.22, 135.17) * mm});
            skSolve(sketch);
        }
        {
            var Q0;
            Q0 = qSketchRegion(id + "F60", true);
            extrude(context, id + "F61", {"entities" : qUnion([Q0]), "depth" : 25.4 * mm, "offsetDistance" : 25.4 * mm});
        }
        {
            var Q0;
            Q0=makeQuery(id+"F55.opExtrude","CAP_FACE",FACE,{"disambiguationData":[OSD([sQuery(id+"F54.wireOp",EDGE,"E60.bottom"),sQuery(id+"F54.wireOp",EDGE,"E60.top"),sQuery(id+"F54.wireOp",EDGE,"E60.left"),sQuery(id+"F54.wireOp",EDGE,"E60.right")])],"isStart":false});
            var sketch = newSketch(context, id + "F62", { "sketchPlane" : qUnion([Q0])});
            skLineSegment(sketch, "E69.bottom", {"start": v(-197.84, 136.03) * mm, "end": v(289.94, 136.03) * mm});
            skLineSegment(sketch, "E69.top", {"start": v(-197.84, -360.04) * mm, "end": v(289.94, -360.04) * mm});
            skLineSegment(sketch, "E69.left", {"start": v(-197.84, 136.03) * mm, "end": v(-197.84, -360.04) * mm});
            skLineSegment(sketch, "E69.right", {"start": v(289.94, 136.03) * mm, "end": v(289.94, -360.04) * mm});
            skCircle(sketch, "E70", {"center": v(47.18, -113.46) * mm, "radius": 114.47 * mm});
            skSolve(sketch);
        }
        {
            var Q0;
            Q0 = qSketchRegion(id + "F62", true);
            extrude(context, id + "F63", {"entities" : qUnion([Q0]), "operationType" : NewBodyOperationType.ADD, "depth" : 25.4 * mm, "offsetDistance" : 25.4 * mm});
        }
        {
            var Q0;
            Q0=makeQuery(id+"F59.opExtrude","CAP_FACE",FACE,{"disambiguationData":[OSD([sQuery(id+"F58.wireOp",EDGE,"E66.bottom"),sQuery(id+"F58.wireOp",EDGE,"E66.top"),sQuery(id+"F58.wireOp",EDGE,"E66.left"),sQuery(id+"F58.wireOp",EDGE,"E66.right"),sQuery(id+"F58.wireOp",EDGE,"E67")])],"isStart":false});
            var sketch = newSketch(context, id + "F64", { "sketchPlane" : qUnion([Q0])});
            skCircle(sketch, "E71", {"center": v(47.18, -113.46) * mm, "radius": 91.78 * mm});
            skLineSegment(sketch, "E72.bottom", {"start": v(-269.36, 135.17) * mm, "end": v(230.38, 135.17) * mm});
            skLineSegment(sketch, "E72.top", {"start": v(-269.36, -353.4) * mm, "end": v(230.38, -353.4) * mm});
            skLineSegment(sketch, "E72.left", {"start": v(-269.36, 135.17) * mm, "end": v(-269.36, -353.4) * mm});
            skLineSegment(sketch, "E72.right", {"start": v(230.38, 135.17) * mm, "end": v(230.38, -353.4) * mm});
            skSolve(sketch);
        }
        {
            var Q0;
            Q0 = qSketchRegion(id + "F64", true);
            extrude(context, id + "F65", {"entities" : qUnion([Q0]), "depth" : 25.4 * mm, "offsetDistance" : 25.4 * mm});
        }
        {
            var Q0;
            Q0=makeQuery(id+"F65.opExtrude","CAP_FACE",FACE,{"disambiguationData":[OSD([sQuery(id+"F64.wireOp",EDGE,"E71"),sQuery(id+"F64.wireOp",EDGE,"E72.bottom"),sQuery(id+"F64.wireOp",EDGE,"E72.top"),sQuery(id+"F64.wireOp",EDGE,"E72.left"),sQuery(id+"F64.wireOp",EDGE,"E72.right")])],"isStart":false});
            var sketch = newSketch(context, id + "F66", { "sketchPlane" : qUnion([Q0])});
            skLineSegment(sketch, "E73.bottom", {"start": v(230.38, 135.17) * mm, "end": v(-102.7, 135.17) * mm});
            skLineSegment(sketch, "E73.top", {"start": v(230.38, -128.03) * mm, "end": v(-102.7, -128.03) * mm});
            skLineSegment(sketch, "E73.left", {"start": v(230.38, 135.17) * mm, "end": v(230.38, -128.03) * mm});
            skLineSegment(sketch, "E73.right", {"start": v(-102.7, 135.17) * mm, "end": v(-102.7, -128.03) * mm});
            skLineSegment(sketch, "E74.bottom", {"start": v(-102.7, 135.17) * mm, "end": v(-269.36, 135.17) * mm});
            skLineSegment(sketch, "E74.top", {"start": v(-102.7, 0) * mm, "end": v(-269.36, 0) * mm});
            skLineSegment(sketch, "E74.left", {"start": v(-102.7, 135.17) * mm, "end": v(-102.7, 0) * mm});
            skLineSegment(sketch, "E74.right", {"start": v(-269.36, 135.17) * mm, "end": v(-269.36, 0) * mm});
            skLineSegment(sketch, "E75.bottom", {"start": v(-102.7, 0) * mm, "end": v(-210.83, 0) * mm});
            skLineSegment(sketch, "E75.top", {"start": v(-102.7, -41.78) * mm, "end": v(-210.83, -41.78) * mm});
            skLineSegment(sketch, "E75.left", {"start": v(-102.7, 0) * mm, "end": v(-102.7, -41.78) * mm});
            skLineSegment(sketch, "E75.right", {"start": v(-210.83, 0) * mm, "end": v(-210.83, -41.78) * mm});
            skSolve(sketch);
        }
        {
            var Q0;
            Q0=makeQuery(id+"F66.imprint","IMPRINT",FACE,{"disambiguationData":[TD([[makeQuery(id+"F66.imprint","IMPRINT",EDGE,{"derivedFrom":sQuery(id+"F66.wireOp",EDGE,"E74.bottom")}),-1.0]])]});
            var Q1;
            {var subQ0=sQuery(id+"F66.wireOp",EDGE,"E73.top");var subQ1=makeQuery(id+"F65.opExtrude","CAP_EDGE",EDGE,{"disambiguationData":[OSD([sQuery(id+"F64.wireOp",EDGE,"E71")])],"isStart":false});var subQ2=makeQuery(id+"F66.imprint","INTERSECT",VERTEX,{"disambiguationData":[OD(0.0)],"derivedFrom":[subQ1,subQ0]});Q1=makeQuery(id+"F66.imprint","IMPRINT",FACE,{"disambiguationData":[TD([[makeQuery(id+"F66.imprint","IMPRINT",EDGE,{"disambiguationData":[TD([[subQ2,-1.0]])],"derivedFrom":subQ0}),-1.0]])]});}
            var Q2;
            Q2=makeQuery(id+"F66.imprint","IMPRINT",FACE,{"disambiguationData":[TD([[makeQuery(id+"F66.imprint","IMPRINT",EDGE,{"derivedFrom":sQuery(id+"F66.wireOp",EDGE,"E75.bottom")}),1.0]])]});
            extrude(context, id + "F67", {"entities" : qUnion([Q0, Q1, Q2]), "operationType" : NewBodyOperationType.ADD, "depth" : 25.4 * mm, "offsetDistance" : 25.4 * mm});
        }
        {
            var Q0;
            Q0=makeQuery(id+"F67.opExtrude","CAP_FACE",FACE,{"disambiguationData":[OSD([sQuery(id+"F64.wireOp",EDGE,"E71"),sQuery(id+"F66.wireOp",EDGE,"E73.top")])],"isStart":false});
            var sketch = newSketch(context, id + "F68", { "sketchPlane" : qUnion([Q0])});
            skLineSegment(sketch, "E76.bottom", {"start": v(299.25, -323.77) * mm, "end": v(70.4, -323.77) * mm});
            skLineSegment(sketch, "E76.top", {"start": v(299.25, 172.27) * mm, "end": v(70.4, 172.27) * mm});
            skLineSegment(sketch, "E76.left", {"start": v(299.25, -323.77) * mm, "end": v(299.25, 172.27) * mm});
            skLineSegment(sketch, "E76.right", {"start": v(70.4, -323.77) * mm, "end": v(70.4, 172.27) * mm});
            skSolve(sketch);
        }
        {
            var Q0;
            {var subQ0=sQuery(id+"F68.wireOp",EDGE,"E76.right");var subQ1=makeQuery(id+"F67.opExtrude","CAP_EDGE",EDGE,{"disambiguationData":[OSD([sQuery(id+"F66.wireOp",EDGE,"E73.top")])],"isStart":false});var subQ2=makeQuery(id+"F68.imprint","INTERSECT",VERTEX,{"derivedFrom":[subQ1,subQ0]});Q0=makeQuery(id+"F68.imprint","IMPRINT",FACE,{"disambiguationData":[TD([[makeQuery(id+"F68.imprint","IMPRINT",EDGE,{"disambiguationData":[TD([[subQ2,-1.0]])],"derivedFrom":subQ0}),-1.0]])]});}
            var Q1;
            {var subQ0=sQuery(id+"F68.wireOp",EDGE,"E76.right");var subQ1=makeQuery(id+"F67.opExtrude","CAP_EDGE",EDGE,{"disambiguationData":[OSD([sQuery(id+"F66.wireOp",EDGE,"E73.top")])],"isStart":false});var subQ2=makeQuery(id+"F68.imprint","INTERSECT",VERTEX,{"derivedFrom":[subQ1,subQ0]});Q1=makeQuery(id+"F68.imprint","IMPRINT",FACE,{"disambiguationData":[TD([[makeQuery(id+"F68.imprint","IMPRINT",EDGE,{"disambiguationData":[TD([[subQ2,-1.0]])],"derivedFrom":subQ0}),1.0]])]});}
            extrude(context, id + "F69", {"entities" : qUnion([Q0, Q1]), "operationType" : NewBodyOperationType.ADD, "depth" : 25.4 * mm, "offsetDistance" : 25.4 * mm});
        }
        {
            var Q0;
            Q0=makeQuery(id+"F55.opExtrude","CAP_FACE",FACE,{"disambiguationData":[OSD([sQuery(id+"F54.wireOp",EDGE,"E60.bottom"),sQuery(id+"F54.wireOp",EDGE,"E60.top"),sQuery(id+"F54.wireOp",EDGE,"E60.left"),sQuery(id+"F54.wireOp",EDGE,"E60.right")])],"isStart":false});
            var sketch = newSketch(context, id + "F70", { "sketchPlane" : qUnion([Q0])});
            skCircle(sketch, "E77", {"center": v(65.98, -83.51) * mm, "radius": 98.11 * mm});
            skLineSegment(sketch, "E78.bottom", {"start": v(294.9, -360.99) * mm, "end": v(-96.07, -360.99) * mm});
            skLineSegment(sketch, "E78.top", {"start": v(294.9, 138.06) * mm, "end": v(-96.07, 138.06) * mm});
            skLineSegment(sketch, "E78.left", {"start": v(294.9, -360.99) * mm, "end": v(294.9, 138.06) * mm});
            skLineSegment(sketch, "E78.right", {"start": v(-96.07, -360.99) * mm, "end": v(-96.07, 138.06) * mm});
            skSolve(sketch);
        }
        {
            var Q0;
            Q0 = qSketchRegion(id + "F70", true);
            extrude(context, id + "F71", {"entities" : qUnion([Q0]), "operationType" : NewBodyOperationType.ADD, "depth" : 25.4 * mm, "offsetDistance" : 25.4 * mm});
        }
        {
            var Q0;
            Q0=makeQuery(id+"F69.opExtrude","CAP_FACE",FACE,{"disambiguationData":[OSD([sQuery(id+"F64.wireOp",EDGE,"E71"),sQuery(id+"F66.wireOp",EDGE,"E73.top")])],"isStart":false});
            var sketch = newSketch(context, id + "F72", { "sketchPlane" : qUnion([Q0])});
            skLineSegment(sketch, "E79.bottom", {"start": v(-199.03, 176.59) * mm, "end": v(297.44, 176.59) * mm});
            skLineSegment(sketch, "E79.top", {"start": v(-199.03, -326.38) * mm, "end": v(297.44, -326.38) * mm});
            skLineSegment(sketch, "E79.left", {"start": v(-199.03, 176.59) * mm, "end": v(-199.03, -326.38) * mm});
            skLineSegment(sketch, "E79.right", {"start": v(297.44, 176.59) * mm, "end": v(297.44, -326.38) * mm});
            skSolve(sketch);
        }
        {
            var Q0;
            Q0 = qSketchRegion(id + "F72", true);
            extrude(context, id + "F73", {"entities" : qUnion([Q0]), "operationType" : NewBodyOperationType.ADD, "depth" : 25.4 * mm, "offsetDistance" : 25.4 * mm});
        }
        {
            var Q0;
            Q0=makeQuery(id+"F73.opExtrude","CAP_FACE",FACE,{"disambiguationData":[OSD([sQuery(id+"F72.wireOp",EDGE,"E79.bottom"),sQuery(id+"F72.wireOp",EDGE,"E79.top"),sQuery(id+"F72.wireOp",EDGE,"E79.left"),sQuery(id+"F72.wireOp",EDGE,"E79.right")])],"isStart":false});
            var sketch = newSketch(context, id + "F74", { "sketchPlane" : qUnion([Q0])});
            skLineSegment(sketch, "E80.bottom", {"start": v(52.64, -73.95) * mm, "end": v(-121.77, -73.95) * mm});
            skLineSegment(sketch, "E80.top", {"start": v(52.64, -273.47) * mm, "end": v(-121.77, -273.47) * mm});
            skLineSegment(sketch, "E80.left", {"start": v(52.64, -73.95) * mm, "end": v(52.64, -273.47) * mm});
            skLineSegment(sketch, "E80.right", {"start": v(-121.77, -73.95) * mm, "end": v(-121.77, -273.47) * mm});
            skLineSegment(sketch, "E81.bottom", {"start": v(-106.12, 0) * mm, "end": v(22.2, 0) * mm});
            skLineSegment(sketch, "E81.top", {"start": v(-106.12, 153.04) * mm, "end": v(22.2, 153.04) * mm});
            skLineSegment(sketch, "E81.left", {"start": v(-106.12, 0) * mm, "end": v(-106.12, 153.04) * mm});
            skLineSegment(sketch, "E81.right", {"start": v(22.2, 0) * mm, "end": v(22.2, 153.04) * mm});
            skLineSegment(sketch, "E82.bottom", {"start": v(160.87, -195.6) * mm, "end": v(226.19, -195.6) * mm});
            skLineSegment(sketch, "E82.top", {"start": v(160.87, -100.13) * mm, "end": v(226.19, -100.13) * mm});
            skLineSegment(sketch, "E82.left", {"start": v(160.87, -195.6) * mm, "end": v(160.87, -100.13) * mm});
            skLineSegment(sketch, "E82.right", {"start": v(226.19, -195.6) * mm, "end": v(226.19, -100.13) * mm});
            skLineSegment(sketch, "E83.bottom", {"start": v(161.45, 0) * mm, "end": v(79.67, 0) * mm});
            skLineSegment(sketch, "E83.top", {"start": v(161.45, -46.97) * mm, "end": v(79.67, -46.97) * mm});
            skLineSegment(sketch, "E83.left", {"start": v(161.45, 0) * mm, "end": v(161.45, -46.97) * mm});
            skLineSegment(sketch, "E83.right", {"start": v(79.67, 0) * mm, "end": v(79.67, -46.97) * mm});
            skPoint(sketch, "E84.oppositeSnap0", {"position": v(161.45, -23.49) * mm});
            skLineSegment(sketch, "E84.bottom", {"start": v(-199.03, -326.38) * mm, "end": v(161.45, -326.38) * mm});
            skLineSegment(sketch, "E84.top", {"start": v(-199.03, 176.59) * mm, "end": v(161.45, 176.59) * mm});
            skLineSegment(sketch, "E84.left", {"start": v(-199.03, -326.38) * mm, "end": v(-199.03, 176.59) * mm});
            skLineSegment(sketch, "E84.right", {"start": v(161.45, -326.38) * mm, "end": v(161.45, 176.59) * mm});
            skLineSegment(sketch, "E85.bottom", {"start": v(161.45, -326.38) * mm, "end": v(226.19, -326.38) * mm});
            skLineSegment(sketch, "E85.top", {"start": v(161.45, -100.13) * mm, "end": v(226.19, -100.13) * mm});
            skLineSegment(sketch, "E85.left", {"start": v(161.45, -326.38) * mm, "end": v(161.45, -100.13) * mm});
            skLineSegment(sketch, "E85.right", {"start": v(226.19, -326.38) * mm, "end": v(226.19, -100.13) * mm});
            skSolve(sketch);
        }
        {
            var Q0;
            Q0 = qSketchRegion(id + "F74", true);
            extrude(context, id + "F75", {"entities" : qUnion([Q0]), "operationType" : NewBodyOperationType.ADD, "depth" : 25.4 * mm, "offsetDistance" : 25.4 * mm});
        }
        {
            var Q0;
            Q0=makeQuery(id+"F75.opExtrude","CAP_FACE",FACE,{"disambiguationData":[OSD([sQuery(id+"F74.wireOp",EDGE,"E80.bottom"),sQuery(id+"F74.wireOp",EDGE,"E80.top"),sQuery(id+"F74.wireOp",EDGE,"E80.left"),sQuery(id+"F74.wireOp",EDGE,"E80.right"),sQuery(id+"F74.wireOp",EDGE,"E81.bottom"),sQuery(id+"F74.wireOp",EDGE,"E81.top"),sQuery(id+"F74.wireOp",EDGE,"E81.left"),sQuery(id+"F74.wireOp",EDGE,"E81.right"),sQuery(id+"F74.wireOp",EDGE,"E84.bottom"),sQuery(id+"F74.wireOp",EDGE,"E84.top"),sQuery(id+"F74.wireOp",EDGE,"E84.left"),sQuery(id+"F74.wireOp",EDGE,"E84.right"),sQuery(id+"F74.wireOp",EDGE,"E85.bottom"),sQuery(id+"F74.wireOp",EDGE,"E85.top"),sQuery(id+"F74.wireOp",EDGE,"E85.right")])],"isStart":false});
            var sketch = newSketch(context, id + "F76", { "sketchPlane" : qUnion([Q0])});
            skLineSegment(sketch, "E86.bottom", {"start": v(-229.85, 171.58) * mm, "end": v(262.6, 171.58) * mm});
            skLineSegment(sketch, "E86.top", {"start": v(-229.85, -326.38) * mm, "end": v(262.6, -326.38) * mm});
            skLineSegment(sketch, "E86.left", {"start": v(-229.85, 171.58) * mm, "end": v(-229.85, -326.38) * mm});
            skLineSegment(sketch, "E86.right", {"start": v(262.6, 171.58) * mm, "end": v(262.6, -326.38) * mm});
            skSolve(sketch);
        }
        {
            var Q0;
            Q0 = qSketchRegion(id + "F76", true);
            extrude(context, id + "F77", {"entities" : qUnion([Q0]), "operationType" : NewBodyOperationType.ADD, "depth" : 25.4 * mm, "offsetDistance" : 25.4 * mm});
        }
        {
            var Q0;
            Q0=makeQuery(id+"F77.opExtrude","CAP_FACE",FACE,{"disambiguationData":[OSD([sQuery(id+"F76.wireOp",EDGE,"E86.bottom"),sQuery(id+"F76.wireOp",EDGE,"E86.top"),sQuery(id+"F76.wireOp",EDGE,"E86.left"),sQuery(id+"F76.wireOp",EDGE,"E86.right")])],"isStart":false});
            var sketch = newSketch(context, id + "F78", { "sketchPlane" : qUnion([Q0])});
            skLineSegment(sketch, "E87.bottom", {"start": v(-29.77, -233.84) * mm, "end": v(95.35, -233.84) * mm});
            skLineSegment(sketch, "E87.top", {"start": v(-29.77, -114.57) * mm, "end": v(95.35, -114.57) * mm});
            skLineSegment(sketch, "E87.left", {"start": v(-29.77, -233.84) * mm, "end": v(-29.77, -114.57) * mm});
            skLineSegment(sketch, "E87.right", {"start": v(95.35, -233.84) * mm, "end": v(95.35, -114.57) * mm});
            skLineSegment(sketch, "E88.bottom", {"start": v(51.31, -186.4) * mm, "end": v(0, -186.4) * mm});
            skLineSegment(sketch, "E88.top", {"start": v(51.31, -114.57) * mm, "end": v(0, -114.57) * mm});
            skLineSegment(sketch, "E88.left", {"start": v(51.31, -186.4) * mm, "end": v(51.31, -114.57) * mm});
            skLineSegment(sketch, "E88.right", {"start": v(0, -186.4) * mm, "end": v(0, -114.57) * mm});
            skPoint(sketch, "E89.firstSnap0", {"position": v(0, -150.49) * mm});
            skLineSegment(sketch, "E89.bottom", {"start": v(19.15, -150.49) * mm, "end": v(32.79, -150.49) * mm});
            skLineSegment(sketch, "E89.top", {"start": v(19.15, -114.57) * mm, "end": v(32.79, -114.57) * mm});
            skLineSegment(sketch, "E89.left", {"start": v(19.15, -150.49) * mm, "end": v(19.15, -114.57) * mm});
            skLineSegment(sketch, "E89.right", {"start": v(32.79, -150.49) * mm, "end": v(32.79, -114.57) * mm});
            skLineSegment(sketch, "E90.bottom", {"start": v(51.31, -233.84) * mm, "end": v(0, -233.84) * mm});
            skLineSegment(sketch, "E90.left", {"start": v(51.31, -233.84) * mm, "end": v(51.31, -186.4) * mm});
            skLineSegment(sketch, "E90.right", {"start": v(0, -233.84) * mm, "end": v(0, -186.4) * mm});
            skSolve(sketch);
        }
        {
            var Q0;
            Q0 = qSketchRegion(id + "F78", true);
            extrude(context, id + "F79", {"entities" : qUnion([Q0]), "operationType" : NewBodyOperationType.ADD, "depth" : 25.4 * mm, "offsetDistance" : 25.4 * mm});
        }
        {
            var Q0;
            Q0=makeQuery(id+"F79.opExtrude","CAP_FACE",FACE,{"disambiguationData":[OSD([sQuery(id+"F78.wireOp",EDGE,"E87.bottom"),sQuery(id+"F78.wireOp",EDGE,"E87.top"),sQuery(id+"F78.wireOp",EDGE,"E87.left"),sQuery(id+"F78.wireOp",EDGE,"E87.right"),sQuery(id+"F78.wireOp",EDGE,"E88.top"),sQuery(id+"F78.wireOp",EDGE,"E89.top"),sQuery(id+"F78.wireOp",EDGE,"E90.bottom")])],"isStart":false});
            var sketch = newSketch(context, id + "F80", { "sketchPlane" : qUnion([Q0])});
            skLineSegment(sketch, "E91.bottom", {"start": v(-215.77, -416.56) * mm, "end": v(283.68, -416.56) * mm});
            skLineSegment(sketch, "E91.top", {"start": v(-215.77, -90.87) * mm, "end": v(283.68, -90.87) * mm});
            skLineSegment(sketch, "E91.left", {"start": v(-215.77, -416.56) * mm, "end": v(-215.77, -90.87) * mm});
            skLineSegment(sketch, "E91.right", {"start": v(283.68, -416.56) * mm, "end": v(283.68, -90.87) * mm});
            skLineSegment(sketch, "E92.bottom", {"start": v(95.35, -233.84) * mm, "end": v(-29.77, -233.84) * mm});
            skLineSegment(sketch, "E92.top", {"start": v(95.35, -114.57) * mm, "end": v(-29.77, -114.57) * mm});
            skLineSegment(sketch, "E92.left", {"start": v(95.35, -233.84) * mm, "end": v(95.35, -114.57) * mm});
            skLineSegment(sketch, "E92.right", {"start": v(-29.77, -233.84) * mm, "end": v(-29.77, -114.57) * mm});
            skSolve(sketch);
        }
        {
            var Q0;
            Q0 = qSketchRegion(id + "F80", true);
            extrude(context, id + "F81", {"entities" : qUnion([Q0]), "depth" : 25.4 * mm, "offsetDistance" : 25.4 * mm});
        }
        {
            var Q0;
            Q0=makeQuery(id+"F81.opExtrude","CAP_FACE",FACE,{"disambiguationData":[OSD([sQuery(id+"F80.wireOp",EDGE,"E91.bottom"),sQuery(id+"F80.wireOp",EDGE,"E91.top"),sQuery(id+"F80.wireOp",EDGE,"E91.left"),sQuery(id+"F80.wireOp",EDGE,"E91.right"),sQuery(id+"F80.wireOp",EDGE,"E92.bottom"),sQuery(id+"F80.wireOp",EDGE,"E92.top"),sQuery(id+"F80.wireOp",EDGE,"E92.left"),sQuery(id+"F80.wireOp",EDGE,"E92.right")])],"isStart":false});
            var sketch = newSketch(context, id + "F82", { "sketchPlane" : qUnion([Q0])});
            skLineSegment(sketch, "E93.bottom", {"start": v(284.98, 0) * mm, "end": v(-211.62, 0) * mm});
            skLineSegment(sketch, "E93.top", {"start": v(284.98, -502.21) * mm, "end": v(-211.62, -502.21) * mm});
            skLineSegment(sketch, "E93.left", {"start": v(284.98, 0) * mm, "end": v(284.98, -502.21) * mm});
            skLineSegment(sketch, "E93.right", {"start": v(-211.62, 0) * mm, "end": v(-211.62, -502.21) * mm});
            skSolve(sketch);
        }
        {
            var Q0;
            Q0 = qSketchRegion(id + "F82", true);
            extrude(context, id + "F83", {"entities" : qUnion([Q0]), "operationType" : NewBodyOperationType.ADD, "depth" : 25.4 * mm, "offsetDistance" : 25.4 * mm});
        }
        {
            var Q0;
            Q0=makeQuery(id+"F39.opExtrude","CAP_FACE",FACE,{"disambiguationData":[OSD([sQuery(id+"F38.wireOp",EDGE,"E50.bottom"),sQuery(id+"F38.wireOp",EDGE,"E50.top"),sQuery(id+"F38.wireOp",EDGE,"E50.left"),sQuery(id+"F38.wireOp",EDGE,"E50.right")])],"isStart":false});
            var sketch = newSketch(context, id + "F84", { "sketchPlane" : qUnion([Q0])});
            skLineSegment(sketch, "E94.bottom", {"start": v(-226.7, -33.19) * mm, "end": v(351.15, -33.19) * mm});
            skLineSegment(sketch, "E94.top", {"start": v(-226.7, 695.8) * mm, "end": v(351.15, 695.8) * mm});
            skLineSegment(sketch, "E94.left", {"start": v(-226.7, -33.19) * mm, "end": v(-226.7, 695.8) * mm});
            skLineSegment(sketch, "E94.right", {"start": v(351.15, -33.19) * mm, "end": v(351.15, 695.8) * mm});
            skLineSegment(sketch, "E95.bottom", {"start": v(-226.7, 463.33) * mm, "end": v(277.6, 463.33) * mm});
            skLineSegment(sketch, "E95.top", {"start": v(-226.7, 37.16) * mm, "end": v(277.6, 37.16) * mm});
            skLineSegment(sketch, "E95.left", {"start": v(-226.7, 463.33) * mm, "end": v(-226.7, 37.16) * mm});
            skLineSegment(sketch, "E95.right", {"start": v(277.6, 463.33) * mm, "end": v(277.6, 37.16) * mm});
            skSolve(sketch);
        }
        {
            var Q0;
            Q0 = qSketchRegion(id + "F84", true);
            extrude(context, id + "F85", {"entities" : qUnion([Q0]), "depth" : 463.1 * mm, "offsetDistance" : 25.4 * mm});
        }
        {
            var Q0;
            Q0=makeQuery(id+"F53.boolean.opBoolean","MERGE",FACE,{"derivedFrom":[makeQuery(id+"F51.boolean.opBoolean","MERGE",FACE,{"derivedFrom":[makeQuery(id+"F49.boolean.opBoolean","MERGE",FACE,{"derivedFrom":[makeQuery(id+"F47.boolean.opBoolean","MERGE",FACE,{"derivedFrom":[makeQuery(id+"F45.boolean.opBoolean","MERGE",FACE,{"derivedFrom":[makeQuery(id+"F43.boolean.opBoolean","MERGE",FACE,{"derivedFrom":[makeQuery(id+"F41.boolean.opBoolean","MERGE",FACE,{"derivedFrom":[makeQuery(id+"F39.opExtrude","SWEPT_FACE",FACE,{"disambiguationData":[OSD([sQuery(id+"F38.wireOp",EDGE,"E50.right")])]}),makeQuery(id+"F41.opExtrude","SWEPT_FACE",FACE,{"disambiguationData":[OSD([sQuery(id+"F40.wireOp",EDGE,"E51.left")])]})]}),makeQuery(id+"F43.opExtrude","SWEPT_FACE",FACE,{"disambiguationData":[OSD([sQuery(id+"F42.wireOp",EDGE,"E52.left")])]})]}),makeQuery(id+"F45.opExtrude","SWEPT_FACE",FACE,{"disambiguationData":[OSD([sQuery(id+"F44.wireOp",EDGE,"E53.left")])]})]}),makeQuery(id+"F47.opExtrude","SWEPT_FACE",FACE,{"disambiguationData":[OSD([sQuery(id+"F46.wireOp",EDGE,"E54.left")])]})]}),makeQuery(id+"F49.opExtrude","SWEPT_FACE",FACE,{"disambiguationData":[OSD([sQuery(id+"F48.wireOp",EDGE,"E55.left")])]})]}),makeQuery(id+"F51.opExtrude","SWEPT_FACE",FACE,{"disambiguationData":[OSD([sQuery(id+"F50.wireOp",EDGE,"E56.right")])]})]}),makeQuery(id+"F53.opExtrude","SWEPT_FACE",FACE,{"disambiguationData":[OSD([sQuery(id+"F52.wireOp",EDGE,"E57.left")])]})]});
            var sketch = newSketch(context, id + "F86", { "sketchPlane" : qUnion([Q0])});
            skLineSegment(sketch, "E96.bottom", {"start": v(753.23, 122.3) * mm, "end": v(68.98, 122.3) * mm});
            skLineSegment(sketch, "E96.top", {"start": v(753.23, -156.72) * mm, "end": v(68.98, -156.72) * mm});
            skLineSegment(sketch, "E96.left", {"start": v(753.23, 122.3) * mm, "end": v(753.23, -156.72) * mm});
            skLineSegment(sketch, "E96.right", {"start": v(68.98, 122.3) * mm, "end": v(68.98, -156.72) * mm});
            skSolve(sketch);
        }
        {
            var Q0;
            Q0 = qSketchRegion(id + "F86", true);
            extrude(context, id + "F87", {"entities" : qUnion([Q0]), "oppositeDirection" : true, "depth" : 18569.28 * mm, "offsetDistance" : 25.4 * mm});
        }
        {
            var Q0;
            Q0=makeQuery(id+"F87.opExtrude","SWEPT_FACE",FACE,{"disambiguationData":[OSD([sQuery(id+"F86.wireOp",EDGE,"E96.bottom")])]});
            var sketch = newSketch(context, id + "F88", { "sketchPlane" : qUnion([Q0])});
            skLineSegment(sketch, "E97.bottom", {"start": v(199.37, 753.23) * mm, "end": v(-3475.1, 753.23) * mm});
            skLineSegment(sketch, "E97.top", {"start": v(199.37, 125.52) * mm, "end": v(-3475.1, 125.52) * mm});
            skLineSegment(sketch, "E97.left", {"start": v(199.37, 753.23) * mm, "end": v(199.37, 125.52) * mm});
            skLineSegment(sketch, "E97.right", {"start": v(-3475.1, 753.23) * mm, "end": v(-3475.1, 125.52) * mm});
            skLineSegment(sketch, "E98.bottom", {"start": v(-527.1, 68.98) * mm, "end": v(-1790.26, 68.98) * mm});
            skLineSegment(sketch, "E98.top", {"start": v(-527.1, -775.11) * mm, "end": v(-1790.26, -775.11) * mm});
            skLineSegment(sketch, "E98.left", {"start": v(-527.1, 68.98) * mm, "end": v(-527.1, -775.11) * mm});
            skLineSegment(sketch, "E98.right", {"start": v(-1790.26, 68.98) * mm, "end": v(-1790.26, -775.11) * mm});
            skLineSegment(sketch, "E99.bottom", {"start": v(-1566.71, 753.23) * mm, "end": v(-502.68, 753.23) * mm});
            skLineSegment(sketch, "E99.top", {"start": v(-1566.71, 1525.8) * mm, "end": v(-502.68, 1525.8) * mm});
            skLineSegment(sketch, "E99.left", {"start": v(-1566.71, 753.23) * mm, "end": v(-1566.71, 1525.8) * mm});
            skLineSegment(sketch, "E99.right", {"start": v(-502.68, 753.23) * mm, "end": v(-502.68, 1525.8) * mm});
            skSolve(sketch);
        }
        {
            var Q0;
            Q0 = qSketchRegion(id + "F88", true);
            extrude(context, id + "F89", {"entities" : qUnion([Q0]), "oppositeDirection" : true, "depth" : 110994.8 * mm, "offsetDistance" : 25.4 * mm});
        }
        {
            var Q0;
            Q0=makeQuery(id+"F89.opExtrude","SWEPT_FACE",FACE,{"disambiguationData":[OSD([sQuery(id+"F88.wireOp",EDGE,"E97.top")])]});
            var sketch = newSketch(context, id + "F90", { "sketchPlane" : qUnion([Q0])});
            skLineSegment(sketch, "E100.bottom", {"start": v(7921.04, -37368.5) * mm, "end": v(27451.07, -37368.5) * mm});
            skLineSegment(sketch, "E100.top", {"start": v(7921.04, -68105.01) * mm, "end": v(27451.07, -68105.01) * mm});
            skLineSegment(sketch, "E100.left", {"start": v(7921.04, -37368.5) * mm, "end": v(7921.04, -68105.01) * mm});
            skLineSegment(sketch, "E100.right", {"start": v(27451.07, -37368.5) * mm, "end": v(27451.07, -68105.01) * mm});
            skLineSegment(sketch, "E101.bottom", {"start": v(-13879.7, -6178.1) * mm, "end": v(-48274.3, -6178.1) * mm});
            skLineSegment(sketch, "E101.top", {"start": v(-13879.7, 42185.1) * mm, "end": v(-48274.3, 42185.1) * mm});
            skLineSegment(sketch, "E101.left", {"start": v(-13879.7, -6178.1) * mm, "end": v(-13879.7, 42185.1) * mm});
            skLineSegment(sketch, "E101.right", {"start": v(-48274.3, -6178.1) * mm, "end": v(-48274.3, 42185.1) * mm});
            skSolve(sketch);
        }
        {
            var Q0;
            Q0 = qSketchRegion(id + "F90", true);
            extrude(context, id + "F91", {"entities" : qUnion([Q0]), "operationType" : NewBodyOperationType.ADD, "depth" : 25.4 * mm, "offsetDistance" : 25.4 * mm});
        }
        {
            var Q0;
            Q0=makeQuery(id+"F91.opExtrude","CAP_FACE",FACE,{"disambiguationData":[OSD([sQuery(id+"F90.wireOp",EDGE,"E100.bottom"),sQuery(id+"F90.wireOp",EDGE,"E100.top"),sQuery(id+"F90.wireOp",EDGE,"E100.left"),sQuery(id+"F90.wireOp",EDGE,"E100.right")])],"isStart":true});
            var sketch = newSketch(context, id + "F92", { "sketchPlane" : qUnion([Q0])});
            skLineSegment(sketch, "E102.bottom", {"start": v(-9235.14, -44482.9) * mm, "end": v(-26213.62, -44482.9) * mm});
            skLineSegment(sketch, "E102.top", {"start": v(-9235.14, -61231.78) * mm, "end": v(-26213.62, -61231.78) * mm});
            skLineSegment(sketch, "E102.left", {"start": v(-9235.14, -44482.9) * mm, "end": v(-9235.14, -61231.78) * mm});
            skLineSegment(sketch, "E102.right", {"start": v(-26213.62, -44482.9) * mm, "end": v(-26213.62, -61231.78) * mm});
            skSolve(sketch);
        }
        {
            var Q0;
            Q0 = qSketchRegion(id + "F92", true);
            extrude(context, id + "F93", {"entities" : qUnion([Q0]), "operationType" : NewBodyOperationType.ADD, "depth" : 25.4 * mm, "offsetDistance" : 25.4 * mm});
        }
        {
            var Q0;
            Q0=makeQuery(id+"F91.opExtrude","CAP_FACE",FACE,{"disambiguationData":[OSD([sQuery(id+"F90.wireOp",EDGE,"E100.bottom"),sQuery(id+"F90.wireOp",EDGE,"E100.top"),sQuery(id+"F90.wireOp",EDGE,"E100.left"),sQuery(id+"F90.wireOp",EDGE,"E100.right")])],"isStart":true});
            var sketch = newSketch(context, id + "F94", { "sketchPlane" : qUnion([Q0])});
            skLineSegment(sketch, "E103.bottom", {"start": v(-7921.04, -64723.53) * mm, "end": v(0, -64723.53) * mm});
            skLineSegment(sketch, "E103.top", {"start": v(-7921.04, -61231.78) * mm, "end": v(0, -61231.78) * mm});
            skLineSegment(sketch, "E103.left", {"start": v(-7921.04, -64723.53) * mm, "end": v(-7921.04, -61231.78) * mm});
            skLineSegment(sketch, "E103.right", {"start": v(0, -64723.53) * mm, "end": v(0, -61231.78) * mm});
            skPoint(sketch, "E104.oppositeSnap0", {"position": v(-7921.04, -52736.76) * mm});
            skLineSegment(sketch, "E104.bottom", {"start": v(-7921.04, -55489.08) * mm, "end": v(0, -55489.08) * mm});
            skLineSegment(sketch, "E104.top", {"start": v(-7921.04, -52736.76) * mm, "end": v(0, -52736.76) * mm});
            skLineSegment(sketch, "E104.left", {"start": v(-7921.04, -55489.08) * mm, "end": v(-7921.04, -52736.76) * mm});
            skLineSegment(sketch, "E104.right", {"start": v(0, -55489.08) * mm, "end": v(0, -52736.76) * mm});
            skSolve(sketch);
        }
        {
            var Q0;
            Q0 = qSketchRegion(id + "F94", true);
            extrude(context, id + "F95", {"entities" : qUnion([Q0]), "operationType" : NewBodyOperationType.ADD, "depth" : 25.4 * mm, "offsetDistance" : 25.4 * mm});
        }
        {
            var Q0;
            Q0=makeQuery(id+"F91.opExtrude","CAP_FACE",FACE,{"disambiguationData":[OSD([sQuery(id+"F90.wireOp",EDGE,"E101.bottom"),sQuery(id+"F90.wireOp",EDGE,"E101.top"),sQuery(id+"F90.wireOp",EDGE,"E101.left"),sQuery(id+"F90.wireOp",EDGE,"E101.right")])],"isStart":true});
            var sketch = newSketch(context, id + "F96", { "sketchPlane" : qUnion([Q0])});
            skLineSegment(sketch, "E105.bottom", {"start": v(13879.7, 42185.1) * mm, "end": v(7628.07, 42185.1) * mm});
            skLineSegment(sketch, "E105.top", {"start": v(13879.7, -5496.8) * mm, "end": v(7628.07, -5496.8) * mm});
            skLineSegment(sketch, "E105.left", {"start": v(13879.7, 42185.1) * mm, "end": v(13879.7, -5496.8) * mm});
            skLineSegment(sketch, "E105.right", {"start": v(7628.07, 42185.1) * mm, "end": v(7628.07, -5496.8) * mm});
            skLineSegment(sketch, "E106.bottom", {"start": v(13879.7, -6178.1) * mm, "end": v(55209.18, -6178.1) * mm});
            skLineSegment(sketch, "E106.top", {"start": v(13879.7, 41500.96) * mm, "end": v(55209.18, 41500.96) * mm});
            skLineSegment(sketch, "E106.left", {"start": v(13879.7, -6178.1) * mm, "end": v(13879.7, 41500.96) * mm});
            skLineSegment(sketch, "E106.right", {"start": v(55209.18, -6178.1) * mm, "end": v(55209.18, 41500.96) * mm});
            skLineSegment(sketch, "E107.bottom", {"start": v(55209.18, 41500.96) * mm, "end": v(13879.7, 41500.96) * mm});
            skLineSegment(sketch, "E107.top", {"start": v(55209.18, 42185.1) * mm, "end": v(13879.7, 42185.1) * mm});
            skLineSegment(sketch, "E107.left", {"start": v(55209.18, 41500.96) * mm, "end": v(55209.18, 42185.1) * mm});
            skLineSegment(sketch, "E107.right", {"start": v(13879.7, 41500.96) * mm, "end": v(13879.7, 42185.1) * mm});
            skLineSegment(sketch, "E108.bottom", {"start": v(13879.7, -6178.1) * mm, "end": v(7628.07, -6178.1) * mm});
            skLineSegment(sketch, "E108.left", {"start": v(13879.7, -6178.1) * mm, "end": v(13879.7, -5496.8) * mm});
            skLineSegment(sketch, "E108.right", {"start": v(7628.07, -6178.1) * mm, "end": v(7628.07, -5496.8) * mm});
            skLineSegment(sketch, "E109.bottom", {"start": v(37269.66, 18098.98) * mm, "end": v(21389.47, 18098.98) * mm});
            skLineSegment(sketch, "E109.top", {"start": v(37269.66, -1736.91) * mm, "end": v(21389.47, -1736.91) * mm});
            skLineSegment(sketch, "E109.left", {"start": v(37269.66, 18098.98) * mm, "end": v(37269.66, -1736.91) * mm});
            skLineSegment(sketch, "E109.right", {"start": v(21389.47, 18098.98) * mm, "end": v(21389.47, -1736.91) * mm});
            skLineSegment(sketch, "E110.bottom", {"start": v(34268.46, 36470.2) * mm, "end": v(21963.71, 36470.2) * mm});
            skLineSegment(sketch, "E110.top", {"start": v(34268.46, 20794.9) * mm, "end": v(21963.71, 20794.9) * mm});
            skLineSegment(sketch, "E110.left", {"start": v(34268.46, 36470.2) * mm, "end": v(34268.46, 20794.9) * mm});
            skLineSegment(sketch, "E110.right", {"start": v(21963.71, 36470.2) * mm, "end": v(21963.71, 20794.9) * mm});
            skSolve(sketch);
        }
        {
            var Q0;
            Q0 = qSketchRegion(id + "F96", true);
            extrude(context, id + "F97", {"entities" : qUnion([Q0]), "operationType" : NewBodyOperationType.ADD, "depth" : 25.4 * mm, "offsetDistance" : 25.4 * mm});
        }
        {
            var Q0;
            Q0=makeQuery(id+"F91.opExtrude","CAP_FACE",FACE,{"disambiguationData":[OSD([sQuery(id+"F90.wireOp",EDGE,"E101.bottom"),sQuery(id+"F90.wireOp",EDGE,"E101.top"),sQuery(id+"F90.wireOp",EDGE,"E101.left"),sQuery(id+"F90.wireOp",EDGE,"E101.right")])],"isStart":false});
            var Q1;
            Q1=makeQuery(id+"F91.opExtrude","CAP_FACE",FACE,{"disambiguationData":[OSD([sQuery(id+"F90.wireOp",EDGE,"E101.bottom"),sQuery(id+"F90.wireOp",EDGE,"E101.top"),sQuery(id+"F90.wireOp",EDGE,"E101.left"),sQuery(id+"F90.wireOp",EDGE,"E101.right")])],"isStart":false});
            var sketch = newSketch(context, id + "F98", { "sketchPlane" : qUnion([Q0, Q1])});
            skLineSegment(sketch, "E111.bottom", {"start": v(-37358.1, 18309.32) * mm, "end": v(-21251.85, 18309.32) * mm});
            skLineSegment(sketch, "E111.top", {"start": v(-37358.1, -1979.96) * mm, "end": v(-21251.85, -1979.96) * mm});
            skLineSegment(sketch, "E111.left", {"start": v(-37358.1, 18309.32) * mm, "end": v(-37358.1, -1979.96) * mm});
            skLineSegment(sketch, "E111.right", {"start": v(-21251.85, 18309.32) * mm, "end": v(-21251.85, -1979.96) * mm});
            skLineSegment(sketch, "E112.bottom", {"start": v(-33413.42, 18309.32) * mm, "end": v(-21813.36, 18309.32) * mm});
            skLineSegment(sketch, "E112.top", {"start": v(-33413.42, 36622.67) * mm, "end": v(-21813.36, 36622.67) * mm});
            skLineSegment(sketch, "E112.left", {"start": v(-33413.42, 18309.32) * mm, "end": v(-33413.42, 36622.67) * mm});
            skLineSegment(sketch, "E112.right", {"start": v(-21813.36, 18309.32) * mm, "end": v(-21813.36, 36622.67) * mm});
            skLineSegment(sketch, "E113.bottom", {"start": v(-33413.42, 20522.43) * mm, "end": v(-35332.05, 20522.43) * mm});
            skLineSegment(sketch, "E113.top", {"start": v(-33413.42, 36622.67) * mm, "end": v(-35332.05, 36622.67) * mm});
            skLineSegment(sketch, "E113.left", {"start": v(-33413.42, 20522.43) * mm, "end": v(-33413.42, 36622.67) * mm});
            skLineSegment(sketch, "E113.right", {"start": v(-35332.05, 20522.43) * mm, "end": v(-35332.05, 36622.67) * mm});
            skSolve(sketch);
        }
        {
            var Q0;
            Q0 = qSketchRegion(id + "F98", true);
            extrude(context, id + "F99", {"entities" : qUnion([Q0]), "operationType" : NewBodyOperationType.ADD, "depth" : 25.4 * mm, "offsetDistance" : 25.4 * mm});
        }
        {
            var Q0;
            Q0=makeQuery(id+"F91.opExtrude","CAP_FACE",FACE,{"disambiguationData":[OSD([sQuery(id+"F90.wireOp",EDGE,"E101.bottom"),sQuery(id+"F90.wireOp",EDGE,"E101.top"),sQuery(id+"F90.wireOp",EDGE,"E101.left"),sQuery(id+"F90.wireOp",EDGE,"E101.right")])],"isStart":false});
            var sketch = newSketch(context, id + "F100", { "sketchPlane" : qUnion([Q0])});
            skLineSegment(sketch, "E114.bottom", {"start": v(-661.82, -113109.36) * mm, "end": v(-5560.83, -113109.36) * mm});
            skLineSegment(sketch, "E114.top", {"start": v(-661.82, -100561.74) * mm, "end": v(-5560.83, -100561.74) * mm});
            skLineSegment(sketch, "E114.left", {"start": v(-661.82, -113109.36) * mm, "end": v(-661.82, -100561.74) * mm});
            skLineSegment(sketch, "E114.right", {"start": v(-5560.83, -113109.36) * mm, "end": v(-5560.83, -100561.74) * mm});
            skLineSegment(sketch, "E115.bottom", {"start": v(-661.82, -113109.36) * mm, "end": v(3423.07, -113109.36) * mm});
            skLineSegment(sketch, "E115.top", {"start": v(-661.82, -101168.37) * mm, "end": v(3423.07, -101168.37) * mm});
            skLineSegment(sketch, "E115.left", {"start": v(-661.82, -113109.36) * mm, "end": v(-661.82, -101168.37) * mm});
            skLineSegment(sketch, "E115.right", {"start": v(3423.07, -113109.36) * mm, "end": v(3423.07, -101168.37) * mm});
            skLineSegment(sketch, "E116.bottom", {"start": v(3423.07, -113109.36) * mm, "end": v(-5271.32, -113109.36) * mm});
            skLineSegment(sketch, "E116.top", {"start": v(3423.07, -124945.37) * mm, "end": v(-5271.32, -124945.37) * mm});
            skLineSegment(sketch, "E116.left", {"start": v(3423.07, -113109.36) * mm, "end": v(3423.07, -124945.37) * mm});
            skLineSegment(sketch, "E116.right", {"start": v(-5271.32, -113109.36) * mm, "end": v(-5271.32, -124945.37) * mm});
            skLineSegment(sketch, "E117.bottom", {"start": v(-661.82, -113109.36) * mm, "end": v(-661.82, -113109.36) * mm});
            skLineSegment(sketch, "E117.top", {"start": v(-661.82, -122015.03) * mm, "end": v(-661.82, -122015.03) * mm});
            skLineSegment(sketch, "E117.left", {"start": v(-661.82, -113109.36) * mm, "end": v(-661.82, -122015.03) * mm});
            skLineSegment(sketch, "E117.right", {"start": v(-661.82, -113109.36) * mm, "end": v(-661.82, -122015.03) * mm});
            skSolve(sketch);
        }
        {
            var Q0;
            Q0 = qSketchRegion(id + "F100", true);
            extrude(context, id + "F101", {"entities" : qUnion([Q0]), "depth" : 25.4 * mm, "offsetDistance" : 25.4 * mm});
        }
    });
